FCSTD DOCUMENT  (FreeCAD 0.21R33771 (Git))
Label: RING0
License: All rights reserved
LicenseURL: http://en.wikipedia.org/wiki/All_rights_reserved
objects: Part::Part2DObjectPython×336, App::FeaturePython×24, App::DocumentObjectGroup×1
note: 336 computed .brp shape members not serialized (recipe doc carries the construction recipe); baked Part::Feature solids carry a one-line shape summary decoded from their .brp

FEATURE [Part::Part2DObjectPython] Rectangle  # Draft 2D object (typed FeaturePython)
  Area = 0
  ChamferSize = 0
  Columns = 1
  FilletRadius = 0
  Height = 8.42
  Length = 8.42
  MakeFace = false
  Placement = pos=(267.255,-49.5968,0) rot=(0,0,1;6.11518rad)
  Rows = 1
FEATURE [Part::Part2DObjectPython] Circle  # Draft 2D object (typed FeaturePython)
  Area = 0
  FirstAngle = 0
  LastAngle = 0
  MakeFace = false
  Placement = pos=(267.959,-45.446,0) rot=(0,0,1;6.11518rad)
  Radius = 1
FEATURE [Part::Part2DObjectPython] Rectangle001  # Draft 2D object (typed FeaturePython)
  Area = 0
  ChamferSize = 0
  Columns = 1
  FilletRadius = 0
  Height = 6
  Length = 6
  MakeFace = false
  Placement = pos=(269.11,-49.15,0) rot=(0,0,1;0rad)
  Rows = 1
FEATURE [App::FeaturePython] Text  # WARN: FeaturePython — macro-defined, semantics opaque (R4)
  Placement = pos=(270.79,-53.3517,0) rot=(0,0,-1;4.73892rad)
  Text = 0
FEATURE [App::FeaturePython] Text001  # WARN: FeaturePython — macro-defined, semantics opaque (R4)
  Placement = pos=(268.047,49.5386,0) rot=(0,0,1;2.6241rad)
  Text = 6.
FEATURE [Part::Part2DObjectPython] Circle001  # Draft 2D object (typed FeaturePython)
  Area = 3.14159
  FirstAngle = 0
  LastAngle = 0
  MakeFace = true
  Placement = pos=(276.11,-46.15,0) rot=(0,0,1;0rad)
  Radius = 1
FEATURE [Part::Part2DObjectPython] Rectangle002  # Draft 2D object (typed FeaturePython)
  Area = 0
  ChamferSize = 0
  Columns = 1
  FilletRadius = 0
  Height = 8.42
  Length = 8.42
  MakeFace = false
  Placement = pos=(269.616,-34.563,0) rot=(0,0,1;6.17118rad)
  Rows = 1
FEATURE [Part::Part2DObjectPython] Circle002  # Draft 2D object (typed FeaturePython)
  Area = 0
  FirstAngle = 0
  LastAngle = 0
  MakeFace = false
  Placement = pos=(270.086,-30.3794,0) rot=(0,0,1;6.17118rad)
  Radius = 1
FEATURE [Part::Part2DObjectPython] Rectangle003  # Draft 2D object (typed FeaturePython)
  Area = 0
  ChamferSize = 0
  Columns = 1
  FilletRadius = 0
  Height = 6
  Length = 6
  MakeFace = false
  Placement = pos=(271.27,-33.85,0) rot=(0,0,1;0rad)
  Rows = 1
FEATURE [Part::Part2DObjectPython] Circle003  # Draft 2D object (typed FeaturePython)
  Area = 3.14159
  FirstAngle = 0
  LastAngle = 0
  MakeFace = true
  Placement = pos=(278.27,-30.85,0) rot=(0,0,1;0rad)
  Radius = 1
FEATURE [Part::Part2DObjectPython] Rectangle004  # Draft 2D object (typed FeaturePython)
  Area = 0
  ChamferSize = 0
  Columns = 1
  FilletRadius = 0
  Height = 8.42
  Length = 8.42
  MakeFace = false
  Placement = pos=(271.131,-19.4177,0) rot=(0,0,1;6.22718rad)
  Rows = 1
FEATURE [Part::Part2DObjectPython] Circle004  # Draft 2D object (typed FeaturePython)
  Area = 0
  FirstAngle = 0
  LastAngle = 0
  MakeFace = false
  Placement = pos=(271.367,-15.2143,0) rot=(0,0,1;6.22718rad)
  Radius = 1
FEATURE [Part::Part2DObjectPython] Rectangle005  # Draft 2D object (typed FeaturePython)
  Area = 0
  ChamferSize = 0
  Columns = 1
  FilletRadius = 0
  Height = 6
  Length = 6
  MakeFace = false
  Placement = pos=(279.554,-16.9094,0) rot=(0,0,1;2.00503rad)
  Rows = 1
FEATURE [Part::Part2DObjectPython] Circle005  # Draft 2D object (typed FeaturePython)
  Area = 3.14159
  FirstAngle = 0
  LastAngle = 0
  MakeFace = true
  Placement = pos=(273.887,-11.8212,0) rot=(0,0,1;2.00503rad)
  Radius = 1
FEATURE [Part::Part2DObjectPython] Rectangle006  # Draft 2D object (typed FeaturePython)
  Area = 0
  ChamferSize = 0
  Columns = 1
  FilletRadius = 0
  Height = 8.42
  Length = 8.42
  MakeFace = false
  Placement = pos=(271.79,-4.21,0) rot=(0,0,1;0rad)
  Rows = 1
FEATURE [Part::Part2DObjectPython] Circle006  # Draft 2D object (typed FeaturePython)
  Area = 0
  FirstAngle = 0
  LastAngle = 0
  MakeFace = false
  Placement = pos=(271.79,0,0) rot=(0,0,1;0rad)
  Radius = 1
FEATURE [Part::Part2DObjectPython] Rectangle007  # Draft 2D object (typed FeaturePython)
  Area = 0
  ChamferSize = 0
  Columns = 1
  FilletRadius = 0
  Height = 6
  Length = 6
  MakeFace = false
  Placement = pos=(279.954,-1.537,0) rot=(0,0,1;1.98549rad)
  Rows = 1
FEATURE [Part::Part2DObjectPython] Circle007  # Draft 2D object (typed FeaturePython)
  Area = 3.14159
  FirstAngle = 0
  LastAngle = 0
  MakeFace = true
  Placement = pos=(274.388,3.66096,0) rot=(0,0,1;1.98549rad)
  Radius = 1
FEATURE [Part::Part2DObjectPython] Rectangle008  # Draft 2D object (typed FeaturePython)
  Area = 0
  ChamferSize = 0
  Columns = 1
  FilletRadius = 0
  Height = 8.42
  Length = 8.42
  MakeFace = false
  Placement = pos=(271.602,11.0109,0) rot=(0,0,1;0.056007rad)
  Rows = 1
FEATURE [Part::Part2DObjectPython] Circle008  # Draft 2D object (typed FeaturePython)
  Area = 0
  FirstAngle = 0
  LastAngle = 0
  MakeFace = false
  Placement = pos=(271.367,15.2143,0) rot=(0,0,1;0.056007rad)
  Radius = 1
FEATURE [Part::Part2DObjectPython] Rectangle009  # Draft 2D object (typed FeaturePython)
  Area = 0
  ChamferSize = 0
  Columns = 1
  FilletRadius = 0
  Height = 6
  Length = 6
  MakeFace = false
  Placement = pos=(279.425,13.6792,0) rot=(0,0,1;1.92562rad)
  Rows = 1
FEATURE [Part::Part2DObjectPython] Circle009  # Draft 2D object (typed FeaturePython)
  Area = 3.14159
  FirstAngle = 0
  LastAngle = 0
  MakeFace = true
  Placement = pos=(274.18,19.2008,0) rot=(0,0,1;1.92562rad)
  Radius = 1
FEATURE [Part::Part2DObjectPython] Rectangle010  # Draft 2D object (typed FeaturePython)
  Area = 0
  ChamferSize = 0
  Columns = 1
  FilletRadius = 0
  Height = 8.42
  Length = 8.42
  MakeFace = false
  Placement = pos=(270.557,26.1958,0) rot=(0,0,1;0.11201rad)
  Rows = 1
FEATURE [Part::Part2DObjectPython] Circle010  # Draft 2D object (typed FeaturePython)
  Area = 0
  FirstAngle = 0
  LastAngle = 0
  MakeFace = false
  Placement = pos=(270.086,30.3794,0) rot=(0,0,1;0.11201rad)
  Radius = 1
FEATURE [Part::Part2DObjectPython] Rectangle011  # Draft 2D object (typed FeaturePython)
  Area = 0
  ChamferSize = 0
  Columns = 1
  FilletRadius = 0
  Height = 6
  Length = 6
  MakeFace = false
  Placement = pos=(277.955,28.7473,0) rot=(0,0,1;1.83766rad)
  Rows = 1
FEATURE [Part::Part2DObjectPython] Circle011  # Draft 2D object (typed FeaturePython)
  Area = 3.14159
  FirstAngle = 0
  LastAngle = 0
  MakeFace = true
  Placement = pos=(273.215,34.7084,0) rot=(0,0,1;1.83766rad)
  Radius = 1
FEATURE [Part::Part2DObjectPython] Rectangle012  # Draft 2D object (typed FeaturePython)
  Area = 0
  ChamferSize = 0
  Columns = 1
  FilletRadius = 0
  Height = 8.42
  Length = 8.42
  MakeFace = false
  Placement = pos=(268.663,41.2953,0) rot=(0,0,1;0.168002rad)
  Rows = 1
FEATURE [Part::Part2DObjectPython] Circle012  # Draft 2D object (typed FeaturePython)
  Area = 0
  FirstAngle = 0
  LastAngle = 0
  MakeFace = false
  Placement = pos=(267.959,45.446,0) rot=(0,0,1;0.168002rad)
  Radius = 1
FEATURE [Part::Part2DObjectPython] Rectangle013  # Draft 2D object (typed FeaturePython)
  Area = 0
  ChamferSize = 0
  Columns = 1
  FilletRadius = 0
  Height = 6
  Length = 6
  MakeFace = false
  Placement = pos=(275.609,43.7506,0) rot=(0,0,1;1.7551rad)
  Rows = 1
FEATURE [Part::Part2DObjectPython] Circle013  # Draft 2D object (typed FeaturePython)
  Area = 3.14159
  FirstAngle = 0
  LastAngle = 0
  MakeFace = true
  Placement = pos=(271.377,50.0823,0) rot=(0,0,1;1.7551rad)
  Radius = 1
FEATURE [Part::Part2DObjectPython] Rectangle014  # Draft 2D object (typed FeaturePython)
  Area = 0
  ChamferSize = 0
  Columns = 1
  FilletRadius = 0
  Height = 8.42
  Length = 8.42
  MakeFace = false
  Placement = pos=(256.249,90.6777,0) rot=(0,0,1;0.355603rad)
  Rows = 1
FEATURE [Part::Part2DObjectPython] Circle014  # Draft 2D object (typed FeaturePython)
  Area = 0
  FirstAngle = 0
  LastAngle = 0
  MakeFace = false
  Placement = pos=(254.783,94.6243,0) rot=(0,0,1;0.355603rad)
  Radius = 1
FEATURE [Part::Part2DObjectPython] Rectangle015  # Draft 2D object (typed FeaturePython)
  Area = 0
  ChamferSize = 0
  Columns = 1
  FilletRadius = 0
  Height = 6
  Length = 6
  MakeFace = false
  Placement = pos=(262.426,94.0073,0) rot=(0,0,1;1.84307rad)
  Rows = 1
FEATURE [App::FeaturePython] Text002  # WARN: FeaturePython — macro-defined, semantics opaque (R4)
  Placement = pos=(261.188,89.1931,0) rot=(0,0,-1;4.21532rad)
  Text = 0
FEATURE [App::FeaturePython] Text003  # WARN: FeaturePython — macro-defined, semantics opaque (R4)
  Placement = pos=(207.363,176.926,0) rot=(0,0,1;3.1477rad)
  Text = 7
FEATURE [Part::Part2DObjectPython] Circle015  # Draft 2D object (typed FeaturePython)
  Area = 3.14159
  FirstAngle = 0
  LastAngle = 0
  MakeFace = true
  Placement = pos=(257.654,99.9427,0) rot=(0,0,1;1.84307rad)
  Radius = 1
FEATURE [Part::Part2DObjectPython] Rectangle016  # Draft 2D object (typed FeaturePython)
  Area = 0
  ChamferSize = 0
  Columns = 1
  FilletRadius = 0
  Height = 8.42
  Length = 8.42
  MakeFace = false
  Placement = pos=(250.776,104.877,0) rot=(0,0,1;0.411595rad)
  Rows = 1
FEATURE [Part::Part2DObjectPython] Circle016  # Draft 2D object (typed FeaturePython)
  Area = 0
  FirstAngle = 0
  LastAngle = 0
  MakeFace = false
  Placement = pos=(249.092,108.736,0) rot=(0,0,1;0.411595rad)
  Radius = 1
FEATURE [Part::Part2DObjectPython] Rectangle017  # Draft 2D object (typed FeaturePython)
  Area = 0
  ChamferSize = 0
  Columns = 1
  FilletRadius = 0
  Height = 6
  Length = 6
  MakeFace = false
  Placement = pos=(257.005,109.172,0) rot=(0,0,1;2.05774rad)
  Rows = 1
FEATURE [Part::Part2DObjectPython] Circle017  # Draft 2D object (typed FeaturePython)
  Area = 3.14159
  FirstAngle = 0
  LastAngle = 0
  MakeFace = true
  Placement = pos=(251.078,113.955,0) rot=(0,0,1;2.05774rad)
  Radius = 1
FEATURE [Part::Part2DObjectPython] Rectangle018  # Draft 2D object (typed FeaturePython)
  Area = 0
  ChamferSize = 0
  Columns = 1
  FilletRadius = 0
  Height = 8.42
  Length = 8.42
  MakeFace = false
  Placement = pos=(244.51,118.754,0) rot=(0,0,1;0.467617rad)
  Rows = 1
FEATURE [Part::Part2DObjectPython] Circle018  # Draft 2D object (typed FeaturePython)
  Area = 0
  FirstAngle = 0
  LastAngle = 0
  MakeFace = false
  Placement = pos=(242.612,122.512,0) rot=(0,0,1;0.467617rad)
  Radius = 1
FEATURE [Part::Part2DObjectPython] Rectangle019  # Draft 2D object (typed FeaturePython)
  Area = 0
  ChamferSize = 0
  Columns = 1
  FilletRadius = 0
  Height = 6
  Length = 6
  MakeFace = false
  Placement = pos=(250.401,125.732,0) rot=(0,0,1;2.67315rad)
  Rows = 1
FEATURE [Part::Part2DObjectPython] Circle019  # Draft 2D object (typed FeaturePython)
  Area = 3.14159
  FirstAngle = 0
  LastAngle = 0
  MakeFace = true
  Placement = pos=(242.801,126.216,0) rot=(0,0,1;2.67315rad)
  Radius = 1
FEATURE [Part::Part2DObjectPython] Rectangle020  # Draft 2D object (typed FeaturePython)
  Area = 0
  ChamferSize = 0
  Columns = 1
  FilletRadius = 0
  Height = 8.42
  Length = 8.42
  MakeFace = false
  Placement = pos=(237.479,132.249,0) rot=(0,0,1;0.523604rad)
  Rows = 1
FEATURE [Part::Part2DObjectPython] Circle020  # Draft 2D object (typed FeaturePython)
  Area = 0
  FirstAngle = 0
  LastAngle = 0
  MakeFace = false
  Placement = pos=(235.374,135.895,0) rot=(0,0,1;0.523604rad)
  Radius = 1
FEATURE [Part::Part2DObjectPython] Rectangle021  # Draft 2D object (typed FeaturePython)
  Area = 0
  ChamferSize = 0
  Columns = 1
  FilletRadius = 0
  Height = 6
  Length = 6
  MakeFace = false
  Placement = pos=(237.816,142.068,0) rot=(0,0,1;4.21462rad)
  Rows = 1
FEATURE [Part::Part2DObjectPython] Circle021  # Draft 2D object (typed FeaturePython)
  Area = 3.14159
  FirstAngle = 0
  LastAngle = 0
  MakeFace = true
  Placement = pos=(237.11,134.485,0) rot=(0,0,1;4.21462rad)
  Radius = 1
FEATURE [Part::Part2DObjectPython] Rectangle022  # Draft 2D object (typed FeaturePython)
  Area = 0
  ChamferSize = 0
  Columns = 1
  FilletRadius = 0
  Height = 8.42
  Length = 8.42
  MakeFace = false
  Placement = pos=(229.703,145.332,0) rot=(0,0,1;0.579601rad)
  Rows = 1
FEATURE [Part::Part2DObjectPython] Circle022  # Draft 2D object (typed FeaturePython)
  Area = 0
  FirstAngle = 0
  LastAngle = 0
  MakeFace = false
  Placement = pos=(227.398,148.854,0) rot=(0,0,1;0.579601rad)
  Radius = 1
FEATURE [Part::Part2DObjectPython] Rectangle023  # Draft 2D object (typed FeaturePython)
  Area = 0
  ChamferSize = 0
  Columns = 1
  FilletRadius = 0
  Height = 6
  Length = 6
  MakeFace = false
  Placement = pos=(227.695,153.917,0) rot=(0,0,1;4.7904rad)
  Rows = 1
FEATURE [Part::Part2DObjectPython] Circle023  # Draft 2D object (typed FeaturePython)
  Area = 3.14159
  FirstAngle = 0
  LastAngle = 0
  MakeFace = true
  Placement = pos=(231.232,147.172,0) rot=(0,0,1;4.7904rad)
  Radius = 1
FEATURE [Part::Part2DObjectPython] Rectangle024  # Draft 2D object (typed FeaturePython)
  Area = 0
  ChamferSize = 0
  Columns = 1
  FilletRadius = 0
  Height = 8.42
  Length = 8.42
  MakeFace = false
  Placement = pos=(221.211,157.963,0) rot=(0,0,1;0.635602rad)
  Rows = 1
FEATURE [Part::Part2DObjectPython] Circle024  # Draft 2D object (typed FeaturePython)
  Area = 0
  FirstAngle = 0
  LastAngle = 0
  MakeFace = false
  Placement = pos=(218.712,161.351,0) rot=(0,0,1;0.635602rad)
  Radius = 1
FEATURE [Part::Part2DObjectPython] Rectangle025  # Draft 2D object (typed FeaturePython)
  Area = 0
  ChamferSize = 0
  Columns = 1
  FilletRadius = 0
  Height = 6
  Length = 6
  MakeFace = false
  Placement = pos=(218.268,165.67,0) rot=(0,0,1;5.0543rad)
  Rows = 1
FEATURE [Part::Part2DObjectPython] Circle025  # Draft 2D object (typed FeaturePython)
  Area = 3.14159
  FirstAngle = 0
  LastAngle = 0
  MakeFace = true
  Placement = pos=(223.441,160.082,0) rot=(0,0,1;5.0543rad)
  Radius = 1
FEATURE [Part::Part2DObjectPython] Rectangle026  # Draft 2D object (typed FeaturePython)
  Area = 0
  ChamferSize = 0
  Columns = 1
  FilletRadius = 0
  Height = 8.42
  Length = 8.42
  MakeFace = false
  Placement = pos=(212.022,170.092,0) rot=(0,0,1;0.691593rad)
  Rows = 1
FEATURE [Part::Part2DObjectPython] Circle026  # Draft 2D object (typed FeaturePython)
  Area = 0
  FirstAngle = 0
  LastAngle = 0
  MakeFace = false
  Placement = pos=(209.337,173.335,0) rot=(0,0,1;0.691593rad)
  Radius = 1
FEATURE [Part::Part2DObjectPython] Rectangle027  # Draft 2D object (typed FeaturePython)
  Area = 0
  ChamferSize = 0
  Columns = 1
  FilletRadius = 0
  Height = 6
  Length = 6
  MakeFace = false
  Placement = pos=(208.466,177.056,0) rot=(0,0,1;5.251rad)
  Rows = 1
FEATURE [Part::Part2DObjectPython] Circle027  # Draft 2D object (typed FeaturePython)
  Area = 3.14159
  FirstAngle = 0
  LastAngle = 0
  MakeFace = true
  Placement = pos=(214.632,172.586,0) rot=(0,0,1;5.251rad)
  Radius = 1
FEATURE [Part::Part2DObjectPython] Rectangle028  # Draft 2D object (typed FeaturePython)
  Area = 0
  ChamferSize = 0
  Columns = 1
  FilletRadius = 0
  Height = 8.42
  Length = 8.42
  MakeFace = false
  Placement = pos=(176.578,206.652,0) rot=(0,0,1;0.879203rad)
  Rows = 1
FEATURE [Part::Part2DObjectPython] Circle028  # Draft 2D object (typed FeaturePython)
  Area = 0
  FirstAngle = 0
  LastAngle = 0
  MakeFace = false
  Placement = pos=(173.335,209.337,0) rot=(0,0,1;0.879203rad)
  Radius = 1
FEATURE [Part::Part2DObjectPython] Rectangle029  # Draft 2D object (typed FeaturePython)
  Area = 0
  ChamferSize = 0
  Columns = 1
  FilletRadius = 0
  Height = 6
  Length = 6
  MakeFace = false
  Placement = pos=(171.985,211.268,0) rot=(0,0,1;5.81229rad)
  Rows = 1
FEATURE [App::FeaturePython] Text004  # WARN: FeaturePython — macro-defined, semantics opaque (R4)
  Placement = pos=(181.597,207.836,0) rot=(0,0,-1;3.69172rad)
  Text = 0
FEATURE [App::FeaturePython] Text005  # WARN: FeaturePython — macro-defined, semantics opaque (R4)
  Placement = pos=(91.1209,256.902,0) rot=(0,0,1;3.6713rad)
  Text = 8
FEATURE [Part::Part2DObjectPython] Circle029  # Draft 2D object (typed FeaturePython)
  Area = 3.14159
  FirstAngle = 0
  LastAngle = 0
  MakeFace = true
  Placement = pos=(179.585,210.765,0) rot=(0,0,1;5.81229rad)
  Radius = 1
FEATURE [Part::Part2DObjectPython] Rectangle030  # Draft 2D object (typed FeaturePython)
  Area = 0
  ChamferSize = 0
  Columns = 1
  FilletRadius = 0
  Height = 8.42
  Length = 8.42
  MakeFace = false
  Placement = pos=(164.739,216.213,0) rot=(0,0,1;0.935194rad)
  Rows = 1
FEATURE [Part::Part2DObjectPython] Circle030  # Draft 2D object (typed FeaturePython)
  Area = 0
  FirstAngle = 0
  LastAngle = 0
  MakeFace = false
  Placement = pos=(161.351,218.712,0) rot=(0,0,1;0.935194rad)
  Radius = 1
FEATURE [Part::Part2DObjectPython] Rectangle031  # Draft 2D object (typed FeaturePython)
  Area = 0
  ChamferSize = 0
  Columns = 1
  FilletRadius = 0
  Height = 6
  Length = 6
  MakeFace = false
  Placement = pos=(160.075,220.163,0) rot=(0,0,1;5.97182rad)
  Rows = 1
FEATURE [Part::Part2DObjectPython] Circle031  # Draft 2D object (typed FeaturePython)
  Area = 3.14159
  FirstAngle = 0
  LastAngle = 0
  MakeFace = true
  Placement = pos=(167.658,220.875,0) rot=(0,0,1;5.97182rad)
  Radius = 1
FEATURE [Part::Part2DObjectPython] Rectangle032  # Draft 2D object (typed FeaturePython)
  Area = 0
  ChamferSize = 0
  Columns = 1
  FilletRadius = 0
  Height = 8.42
  Length = 8.42
  MakeFace = false
  Placement = pos=(152.377,225.092,0) rot=(0,0,1;0.991195rad)
  Rows = 1
FEATURE [Part::Part2DObjectPython] Circle032  # Draft 2D object (typed FeaturePython)
  Area = 0
  FirstAngle = 0
  LastAngle = 0
  MakeFace = false
  Placement = pos=(148.854,227.398,0) rot=(0,0,1;0.991195rad)
  Radius = 1
FEATURE [Part::Part2DObjectPython] Rectangle033  # Draft 2D object (typed FeaturePython)
  Area = 0
  ChamferSize = 0
  Columns = 1
  FilletRadius = 0
  Height = 6
  Length = 6
  MakeFace = false
  Placement = pos=(147.739,228.41,0) rot=(0,0,1;6.13082rad)
  Rows = 1
FEATURE [Part::Part2DObjectPython] Circle033  # Draft 2D object (typed FeaturePython)
  Area = 3.14159
  FirstAngle = 0
  LastAngle = 0
  MakeFace = true
  Placement = pos=(155.114,230.313,0) rot=(0,0,1;6.13082rad)
  Radius = 1
FEATURE [Part::Part2DObjectPython] Rectangle034  # Draft 2D object (typed FeaturePython)
  Area = 0
  ChamferSize = 0
  Columns = 1
  FilletRadius = 0
  Height = 8.42
  Length = 8.42
  MakeFace = false
  Placement = pos=(139.541,233.269,0) rot=(0,0,1;1.04719rad)
  Rows = 1
FEATURE [Part::Part2DObjectPython] Circle034  # Draft 2D object (typed FeaturePython)
  Area = 0
  FirstAngle = 0
  LastAngle = 0
  MakeFace = false
  Placement = pos=(135.895,235.374,0) rot=(0,0,1;1.04719rad)
  Radius = 1
FEATURE [Part::Part2DObjectPython] Rectangle035  # Draft 2D object (typed FeaturePython)
  Area = 0
  ChamferSize = 0
  Columns = 1
  FilletRadius = 0
  Height = 6
  Length = 6
  MakeFace = false
  Placement = pos=(134.999,236.021,0) rot=(0,0,1;6.28284rad)
  Rows = 1
FEATURE [Part::Part2DObjectPython] Circle035  # Draft 2D object (typed FeaturePython)
  Area = 3.14159
  FirstAngle = 0
  LastAngle = 0
  MakeFace = true
  Placement = pos=(142,239.019,0) rot=(0,0,1;6.28284rad)
  Radius = 1
FEATURE [Part::Part2DObjectPython] Rectangle036  # Draft 2D object (typed FeaturePython)
  Area = 0
  ChamferSize = 0
  Columns = 1
  FilletRadius = 0
  Height = 8.42
  Length = 8.42
  MakeFace = false
  Placement = pos=(126.27,240.714,0) rot=(0,0,1;1.10318rad)
  Rows = 1
FEATURE [Part::Part2DObjectPython] Circle036  # Draft 2D object (typed FeaturePython)
  Area = 0
  FirstAngle = 0
  LastAngle = 0
  MakeFace = false
  Placement = pos=(122.512,242.612,0) rot=(0,0,1;1.10318rad)
  Radius = 1
FEATURE [Part::Part2DObjectPython] Rectangle037  # Draft 2D object (typed FeaturePython)
  Area = 0
  ChamferSize = 0
  Columns = 1
  FilletRadius = 0
  Height = 6
  Length = 6
  MakeFace = false
  Placement = pos=(121.98,242.893,0) rot=(0,0,1;0.175406rad)
  Rows = 1
FEATURE [Part::Part2DObjectPython] Circle037  # Draft 2D object (typed FeaturePython)
  Area = 3.14159
  FirstAngle = 0
  LastAngle = 0
  MakeFace = true
  Placement = pos=(128.349,247.068,0) rot=(0,0,1;0.175406rad)
  Radius = 1
FEATURE [Part::Part2DObjectPython] Rectangle038  # Draft 2D object (typed FeaturePython)
  Area = 0
  ChamferSize = 0
  Columns = 1
  FilletRadius = 0
  Height = 8.42
  Length = 8.42
  MakeFace = false
  Placement = pos=(112.594,247.407,0) rot=(0,0,1;1.1592rad)
  Rows = 1
FEATURE [Part::Part2DObjectPython] Circle038  # Draft 2D object (typed FeaturePython)
  Area = 0
  FirstAngle = 0
  LastAngle = 0
  MakeFace = false
  Placement = pos=(108.736,249.092,0) rot=(0,0,1;1.1592rad)
  Radius = 1
FEATURE [Part::Part2DObjectPython] Rectangle039  # Draft 2D object (typed FeaturePython)
  Area = 0
  ChamferSize = 0
  Columns = 1
  FilletRadius = 0
  Height = 6
  Length = 6
  MakeFace = false
  Placement = pos=(107.42,249.95,0) rot=(0,0,1;0rad)
  Rows = 1
FEATURE [Part::Part2DObjectPython] Circle039  # Draft 2D object (typed FeaturePython)
  Area = 3.14159
  FirstAngle = 0
  LastAngle = 0
  MakeFace = true
  Placement = pos=(114.42,252.95,0) rot=(0,0,1;0rad)
  Radius = 1
FEATURE [Part::Part2DObjectPython] Rectangle040  # Draft 2D object (typed FeaturePython)
  Area = 0
  ChamferSize = 0
  Columns = 1
  FilletRadius = 0
  Height = 8.42
  Length = 8.42
  MakeFace = false
  Placement = pos=(98.5709,253.318,0) rot=(0,0,1;1.21519rad)
  Rows = 1
FEATURE [Part::Part2DObjectPython] Circle040  # Draft 2D object (typed FeaturePython)
  Area = 0
  FirstAngle = 0
  LastAngle = 0
  MakeFace = false
  Placement = pos=(94.6243,254.783,0) rot=(0,0,1;1.21519rad)
  Radius = 1
FEATURE [Part::Part2DObjectPython] Rectangle041  # Draft 2D object (typed FeaturePython)
  Area = 0
  ChamferSize = 0
  Columns = 1
  FilletRadius = 0
  Height = 6
  Length = 6
  MakeFace = false
  Placement = pos=(93.09,255.73,0) rot=(0,0,1;0rad)
  Rows = 1
FEATURE [Part::Part2DObjectPython] Circle041  # Draft 2D object (typed FeaturePython)
  Area = 3.14159
  FirstAngle = 0
  LastAngle = 0
  MakeFace = true
  Placement = pos=(100.09,258.73,0) rot=(0,0,1;0rad)
  Radius = 1
FEATURE [Part::Part2DObjectPython] Rectangle042  # Draft 2D object (typed FeaturePython)
  Area = 0
  ChamferSize = 0
  Columns = 1
  FilletRadius = 0
  Height = 8.42
  Length = 8.42
  MakeFace = false
  Placement = pos=(49.5968,267.255,0) rot=(0,0,1;1.40279rad)
  Rows = 1
FEATURE [Part::Part2DObjectPython] Circle042  # Draft 2D object (typed FeaturePython)
  Area = 0
  FirstAngle = 0
  LastAngle = 0
  MakeFace = false
  Placement = pos=(45.446,267.959,0) rot=(0,0,1;1.40279rad)
  Radius = 1
FEATURE [Part::Part2DObjectPython] Rectangle043  # Draft 2D object (typed FeaturePython)
  Area = 0
  ChamferSize = 0
  Columns = 1
  FilletRadius = 0
  Height = 6
  Length = 6
  MakeFace = false
  Placement = pos=(43.15,269.11,0) rot=(0,0,1;0rad)
  Rows = 1
FEATURE [App::FeaturePython] Text006  # WARN: FeaturePython — macro-defined, semantics opaque (R4)
  Placement = pos=(53.3517,270.79,0) rot=(0,0,-1;3.16812rad)
  Text = 0
FEATURE [App::FeaturePython] Text007  # WARN: FeaturePython — macro-defined, semantics opaque (R4)
  Placement = pos=(-49.5386,268.047,0) rot=(0,0,1;4.1949rad)
  Text = 9
FEATURE [Part::Part2DObjectPython] Circle043  # Draft 2D object (typed FeaturePython)
  Area = 3.14159
  FirstAngle = 0
  LastAngle = 0
  MakeFace = true
  Placement = pos=(50.15,272.11,0) rot=(0,0,1;0rad)
  Radius = 1
FEATURE [Part::Part2DObjectPython] Rectangle044  # Draft 2D object (typed FeaturePython)
  Area = 0
  ChamferSize = 0
  Columns = 1
  FilletRadius = 0
  Height = 8.42
  Length = 8.42
  MakeFace = false
  Placement = pos=(34.563,269.616,0) rot=(0,0,1;1.45879rad)
  Rows = 1
FEATURE [Part::Part2DObjectPython] Circle044  # Draft 2D object (typed FeaturePython)
  Area = 0
  FirstAngle = 0
  LastAngle = 0
  MakeFace = false
  Placement = pos=(30.3794,270.086,0) rot=(0,0,1;1.45879rad)
  Radius = 1
FEATURE [Part::Part2DObjectPython] Rectangle045  # Draft 2D object (typed FeaturePython)
  Area = 0
  ChamferSize = 0
  Columns = 1
  FilletRadius = 0
  Height = 6
  Length = 6
  MakeFace = false
  Placement = pos=(27.85,271.27,0) rot=(0,0,1;0rad)
  Rows = 1
FEATURE [Part::Part2DObjectPython] Circle045  # Draft 2D object (typed FeaturePython)
  Area = 3.14159
  FirstAngle = 0
  LastAngle = 0
  MakeFace = true
  Placement = pos=(34.85,274.27,0) rot=(0,0,1;0rad)
  Radius = 1
FEATURE [Part::Part2DObjectPython] Rectangle046  # Draft 2D object (typed FeaturePython)
  Area = 0
  ChamferSize = 0
  Columns = 1
  FilletRadius = 0
  Height = 8.42
  Length = 8.42
  MakeFace = false
  Placement = pos=(19.4177,271.131,0) rot=(0,0,1;1.51479rad)
  Rows = 1
FEATURE [Part::Part2DObjectPython] Circle046  # Draft 2D object (typed FeaturePython)
  Area = 0
  FirstAngle = 0
  LastAngle = 0
  MakeFace = false
  Placement = pos=(15.2143,271.367,0) rot=(0,0,1;1.51479rad)
  Radius = 1
FEATURE [Part::Part2DObjectPython] Rectangle047  # Draft 2D object (typed FeaturePython)
  Area = 0
  ChamferSize = 0
  Columns = 1
  FilletRadius = 0
  Height = 6
  Length = 6
  MakeFace = false
  Placement = pos=(12.45,272.57,0) rot=(0,0,1;0rad)
  Rows = 1
FEATURE [Part::Part2DObjectPython] Circle047  # Draft 2D object (typed FeaturePython)
  Area = 3.14159
  FirstAngle = 0
  LastAngle = 0
  MakeFace = true
  Placement = pos=(19.45,275.57,0) rot=(0,0,1;0rad)
  Radius = 1
FEATURE [Part::Part2DObjectPython] Rectangle048  # Draft 2D object (typed FeaturePython)
  Area = 0
  ChamferSize = 0
  Columns = 1
  FilletRadius = 0
  Height = 8.42
  Length = 8.42
  MakeFace = false
  Placement = pos=(4.21,271.79,0) rot=(0,0,1;1.5708rad)
  Rows = 1
FEATURE [Part::Part2DObjectPython] Circle048  # Draft 2D object (typed FeaturePython)
  Area = 0
  FirstAngle = 0
  LastAngle = 0
  MakeFace = false
  Placement = pos=(0,271.79,0) rot=(0,0,1;1.5708rad)
  Radius = 1
FEATURE [Part::Part2DObjectPython] Rectangle049  # Draft 2D object (typed FeaturePython)
  Area = 0
  ChamferSize = 0
  Columns = 1
  FilletRadius = 0
  Height = 6
  Length = 6
  MakeFace = false
  Placement = pos=(-3,273,0) rot=(0,0,1;0rad)
  Rows = 1
FEATURE [Part::Part2DObjectPython] Circle049  # Draft 2D object (typed FeaturePython)
  Area = 3.14159
  FirstAngle = 0
  LastAngle = 0
  MakeFace = true
  Placement = pos=(4,276,0) rot=(0,0,1;0rad)
  Radius = 1
FEATURE [Part::Part2DObjectPython] Rectangle050  # Draft 2D object (typed FeaturePython)
  Area = 0
  ChamferSize = 0
  Columns = 1
  FilletRadius = 0
  Height = 8.42
  Length = 8.42
  MakeFace = false
  Placement = pos=(-11.0109,271.602,0) rot=(0,0,1;1.6268rad)
  Rows = 1
FEATURE [Part::Part2DObjectPython] Circle050  # Draft 2D object (typed FeaturePython)
  Area = 0
  FirstAngle = 0
  LastAngle = 0
  MakeFace = false
  Placement = pos=(-15.2143,271.367,0) rot=(0,0,1;1.6268rad)
  Radius = 1
FEATURE [Part::Part2DObjectPython] Rectangle051  # Draft 2D object (typed FeaturePython)
  Area = 0
  ChamferSize = 0
  Columns = 1
  FilletRadius = 0
  Height = 6
  Length = 6
  MakeFace = false
  Placement = pos=(-11.2074,275.547,0) rot=(0,0,1;2.35078rad)
  Rows = 1
FEATURE [Part::Part2DObjectPython] Circle051  # Draft 2D object (typed FeaturePython)
  Area = 3.14159
  FirstAngle = 0
  LastAngle = 0
  MakeFace = true
  Placement = pos=(-18.2631,278.414,0) rot=(0,0,1;2.35078rad)
  Radius = 1
FEATURE [Part::Part2DObjectPython] Rectangle052  # Draft 2D object (typed FeaturePython)
  Area = 0
  ChamferSize = 0
  Columns = 1
  FilletRadius = 0
  Height = 8.42
  Length = 8.42
  MakeFace = false
  Placement = pos=(-26.1958,270.557,0) rot=(0,0,1;1.68281rad)
  Rows = 1
FEATURE [Part::Part2DObjectPython] Circle052  # Draft 2D object (typed FeaturePython)
  Area = 0
  FirstAngle = 0
  LastAngle = 0
  MakeFace = false
  Placement = pos=(-30.3794,270.086,0) rot=(0,0,1;1.68281rad)
  Radius = 1
FEATURE [Part::Part2DObjectPython] Rectangle053  # Draft 2D object (typed FeaturePython)
  Area = 0
  ChamferSize = 0
  Columns = 1
  FilletRadius = 0
  Height = 6
  Length = 6
  MakeFace = false
  Placement = pos=(-26.6143,274.513,0) rot=(0,0,1;2.41344rad)
  Rows = 1
FEATURE [Part::Part2DObjectPython] Circle053  # Draft 2D object (typed FeaturePython)
  Area = 3.14159
  FirstAngle = 0
  LastAngle = 0
  MakeFace = true
  Placement = pos=(-33.8356,276.932,0) rot=(0,0,1;2.41344rad)
  Radius = 1
FEATURE [Part::Part2DObjectPython] Rectangle054  # Draft 2D object (typed FeaturePython)
  Area = 0
  ChamferSize = 0
  Columns = 1
  FilletRadius = 0
  Height = 8.42
  Length = 8.42
  MakeFace = false
  Placement = pos=(-41.2953,268.663,0) rot=(0,0,1;1.7388rad)
  Rows = 1
FEATURE [Part::Part2DObjectPython] Circle054  # Draft 2D object (typed FeaturePython)
  Area = 0
  FirstAngle = 0
  LastAngle = 0
  MakeFace = false
  Placement = pos=(-45.446,267.959,0) rot=(0,0,1;1.7388rad)
  Radius = 1
FEATURE [Part::Part2DObjectPython] Rectangle055  # Draft 2D object (typed FeaturePython)
  Area = 0
  ChamferSize = 0
  Columns = 1
  FilletRadius = 0
  Height = 6
  Length = 6
  MakeFace = false
  Placement = pos=(-41.9327,272.573,0) rot=(0,0,1;2.46545rad)
  Rows = 1
FEATURE [Part::Part2DObjectPython] Circle055  # Draft 2D object (typed FeaturePython)
  Area = 3.14159
  FirstAngle = 0
  LastAngle = 0
  MakeFace = true
  Placement = pos=(-49.27,274.613,0) rot=(0,0,1;2.46545rad)
  Radius = 1
FEATURE [Part::Part2DObjectPython] Rectangle056  # Draft 2D object (typed FeaturePython)
  Area = 0
  ChamferSize = 0
  Columns = 1
  FilletRadius = 0
  Height = 8.42
  Length = 8.42
  MakeFace = false
  Placement = pos=(-90.6777,256.249,0) rot=(0,0,1;1.9264rad)
  Rows = 1
FEATURE [Part::Part2DObjectPython] Circle056  # Draft 2D object (typed FeaturePython)
  Area = 0
  FirstAngle = 0
  LastAngle = 0
  MakeFace = false
  Placement = pos=(-94.6243,254.783,0) rot=(0,0,1;1.9264rad)
  Radius = 1
FEATURE [Part::Part2DObjectPython] Rectangle057  # Draft 2D object (typed FeaturePython)
  Area = 0
  ChamferSize = 0
  Columns = 1
  FilletRadius = 0
  Height = 6
  Length = 6
  MakeFace = false
  Placement = pos=(-92.1068,260.191,0) rot=(0,0,1;2.7077rad)
  Rows = 1
FEATURE [App::FeaturePython] Text008  # WARN: FeaturePython — macro-defined, semantics opaque (R4)
  Placement = pos=(-89.1931,261.188,0) rot=(0,0,-1;2.64452rad)
  Text = 0
FEATURE [App::FeaturePython] Text009  # WARN: FeaturePython — macro-defined, semantics opaque (R4)
  Placement = pos=(-176.926,207.363,0) rot=(0,0,1;4.7185rad)
  Text = 10
FEATURE [Part::Part2DObjectPython] Circle057  # Draft 2D object (typed FeaturePython)
  Area = 3.14159
  FirstAngle = 0
  LastAngle = 0
  MakeFace = true
  Placement = pos=(-99.7194,260.412,0) rot=(0,0,1;2.7077rad)
  Radius = 1
FEATURE [Part::Part2DObjectPython] Rectangle058  # Draft 2D object (typed FeaturePython)
  Area = 0
  ChamferSize = 0
  Columns = 1
  FilletRadius = 0
  Height = 8.42
  Length = 8.42
  MakeFace = false
  Placement = pos=(-104.877,250.776,0) rot=(0,0,1;1.98239rad)
  Rows = 1
FEATURE [Part::Part2DObjectPython] Circle058  # Draft 2D object (typed FeaturePython)
  Area = 0
  FirstAngle = 0
  LastAngle = 0
  MakeFace = false
  Placement = pos=(-108.736,249.092,0) rot=(0,0,1;1.98239rad)
  Radius = 1
FEATURE [Part::Part2DObjectPython] Rectangle059  # Draft 2D object (typed FeaturePython)
  Area = 0
  ChamferSize = 0
  Columns = 1
  FilletRadius = 0
  Height = 6
  Length = 6
  MakeFace = false
  Placement = pos=(-106.607,254.81,0) rot=(0,0,1;2.80998rad)
  Rows = 1
FEATURE [Part::Part2DObjectPython] Circle059  # Draft 2D object (typed FeaturePython)
  Area = 3.14159
  FirstAngle = 0
  LastAngle = 0
  MakeFace = true
  Placement = pos=(-114.202,254.252,0) rot=(0,0,1;2.80998rad)
  Radius = 1
FEATURE [Part::Part2DObjectPython] Rectangle060  # Draft 2D object (typed FeaturePython)
  Area = 0
  ChamferSize = 0
  Columns = 1
  FilletRadius = 0
  Height = 8.42
  Length = 8.42
  MakeFace = false
  Placement = pos=(-118.754,244.51,0) rot=(0,0,1;2.03841rad)
  Rows = 1
FEATURE [Part::Part2DObjectPython] Circle060  # Draft 2D object (typed FeaturePython)
  Area = 0
  FirstAngle = 0
  LastAngle = 0
  MakeFace = false
  Placement = pos=(-122.512,242.612,0) rot=(0,0,1;2.03841rad)
  Radius = 1
FEATURE [Part::Part2DObjectPython] Rectangle061  # Draft 2D object (typed FeaturePython)
  Area = 0
  ChamferSize = 0
  Columns = 1
  FilletRadius = 0
  Height = 6
  Length = 6
  MakeFace = false
  Placement = pos=(-120.843,248.666,0) rot=(0,0,1;2.92814rad)
  Rows = 1
FEATURE [Part::Part2DObjectPython] Circle061  # Draft 2D object (typed FeaturePython)
  Area = 3.14159
  FirstAngle = 0
  LastAngle = 0
  MakeFace = true
  Placement = pos=(-128.319,247.217,0) rot=(0,0,1;2.92814rad)
  Radius = 1
FEATURE [Part::Part2DObjectPython] Rectangle062  # Draft 2D object (typed FeaturePython)
  Area = 0
  ChamferSize = 0
  Columns = 1
  FilletRadius = 0
  Height = 8.42
  Length = 8.42
  MakeFace = false
  Placement = pos=(-132.249,237.479,0) rot=(0,0,1;2.0944rad)
  Rows = 1
FEATURE [Part::Part2DObjectPython] Circle062  # Draft 2D object (typed FeaturePython)
  Area = 0
  FirstAngle = 0
  LastAngle = 0
  MakeFace = false
  Placement = pos=(-135.895,235.374,0) rot=(0,0,1;2.0944rad)
  Radius = 1
FEATURE [Part::Part2DObjectPython] Rectangle063  # Draft 2D object (typed FeaturePython)
  Area = 0
  ChamferSize = 0
  Columns = 1
  FilletRadius = 0
  Height = 6
  Length = 6
  MakeFace = false
  Placement = pos=(-134.775,241.777,0) rot=(0,0,1;3.06358rad)
  Rows = 1
FEATURE [Part::Part2DObjectPython] Circle063  # Draft 2D object (typed FeaturePython)
  Area = 3.14159
  FirstAngle = 0
  LastAngle = 0
  MakeFace = true
  Placement = pos=(-141.988,239.332,0) rot=(0,0,1;3.06358rad)
  Radius = 1
FEATURE [Part::Part2DObjectPython] Rectangle064  # Draft 2D object (typed FeaturePython)
  Area = 0
  ChamferSize = 0
  Columns = 1
  FilletRadius = 0
  Height = 8.42
  Length = 8.42
  MakeFace = false
  Placement = pos=(-145.332,229.703,0) rot=(0,0,1;2.1504rad)
  Rows = 1
FEATURE [Part::Part2DObjectPython] Circle064  # Draft 2D object (typed FeaturePython)
  Area = 0
  FirstAngle = 0
  LastAngle = 0
  MakeFace = false
  Placement = pos=(-148.854,227.398,0) rot=(0,0,1;2.1504rad)
  Radius = 1
FEATURE [Part::Part2DObjectPython] Rectangle065  # Draft 2D object (typed FeaturePython)
  Area = 0
  ChamferSize = 0
  Columns = 1
  FilletRadius = 0
  Height = 6
  Length = 6
  MakeFace = false
  Placement = pos=(-148.392,234.135,0) rot=(0,0,1;3.21612rad)
  Rows = 1
FEATURE [Part::Part2DObjectPython] Circle065  # Draft 2D object (typed FeaturePython)
  Area = 3.14159
  FirstAngle = 0
  LastAngle = 0
  MakeFace = true
  Placement = pos=(-155.149,230.622,0) rot=(0,0,1;3.21612rad)
  Radius = 1
FEATURE [Part::Part2DObjectPython] Rectangle066  # Draft 2D object (typed FeaturePython)
  Area = 0
  ChamferSize = 0
  Columns = 1
  FilletRadius = 0
  Height = 8.42
  Length = 8.42
  MakeFace = false
  Placement = pos=(-157.963,221.211,0) rot=(0,0,1;2.2064rad)
  Rows = 1
FEATURE [Part::Part2DObjectPython] Circle066  # Draft 2D object (typed FeaturePython)
  Area = 0
  FirstAngle = 0
  LastAngle = 0
  MakeFace = false
  Placement = pos=(-161.351,218.712,0) rot=(0,0,1;2.2064rad)
  Radius = 1
FEATURE [Part::Part2DObjectPython] Rectangle067  # Draft 2D object (typed FeaturePython)
  Area = 0
  ChamferSize = 0
  Columns = 1
  FilletRadius = 0
  Height = 6
  Length = 6
  MakeFace = false
  Placement = pos=(-161.674,225.742,0) rot=(0,0,1;3.38838rad)
  Rows = 1
FEATURE [Part::Part2DObjectPython] Circle067  # Draft 2D object (typed FeaturePython)
  Area = 3.14159
  FirstAngle = 0
  LastAngle = 0
  MakeFace = true
  Placement = pos=(-167.729,221.123,0) rot=(0,0,1;3.38838rad)
  Radius = 1
FEATURE [Part::Part2DObjectPython] Rectangle068  # Draft 2D object (typed FeaturePython)
  Area = 0
  ChamferSize = 0
  Columns = 1
  FilletRadius = 0
  Height = 8.42
  Length = 8.42
  MakeFace = false
  Placement = pos=(-170.092,212.022,0) rot=(0,0,1;2.26239rad)
  Rows = 1
FEATURE [Part::Part2DObjectPython] Circle068  # Draft 2D object (typed FeaturePython)
  Area = 0
  FirstAngle = 0
  LastAngle = 0
  MakeFace = false
  Placement = pos=(-173.335,209.337,0) rot=(0,0,1;2.26239rad)
  Radius = 1
FEATURE [Part::Part2DObjectPython] Rectangle069  # Draft 2D object (typed FeaturePython)
  Area = 0
  ChamferSize = 0
  Columns = 1
  FilletRadius = 0
  Height = 6
  Length = 6
  MakeFace = false
  Placement = pos=(-174.591,216.575,0) rot=(0,0,1;3.58351rad)
  Rows = 1
FEATURE [Part::Part2DObjectPython] Circle069  # Draft 2D object (typed FeaturePython)
  Area = 3.14159
  FirstAngle = 0
  LastAngle = 0
  MakeFace = true
  Placement = pos=(-179.636,210.869,0) rot=(0,0,1;3.58351rad)
  Radius = 1
FEATURE [Part::Part2DObjectPython] Rectangle070  # Draft 2D object (typed FeaturePython)
  Area = 0
  ChamferSize = 0
  Columns = 1
  FilletRadius = 0
  Height = 8.42
  Length = 8.42
  MakeFace = false
  Placement = pos=(-206.652,176.578,0) rot=(0,0,1;2.45rad)
  Rows = 1
FEATURE [Part::Part2DObjectPython] Circle070  # Draft 2D object (typed FeaturePython)
  Area = 0
  FirstAngle = 0
  LastAngle = 0
  MakeFace = false
  Placement = pos=(-209.337,173.335,0) rot=(0,0,1;2.45rad)
  Radius = 1
FEATURE [Part::Part2DObjectPython] Rectangle071  # Draft 2D object (typed FeaturePython)
  Area = 0
  ChamferSize = 0
  Columns = 1
  FilletRadius = 0
  Height = 6
  Length = 6
  MakeFace = false
  Placement = pos=(-215.58,173.02,0) rot=(0,0,1;0rad)
  Rows = 1
FEATURE [App::FeaturePython] Text010  # WARN: FeaturePython — macro-defined, semantics opaque (R4)
  Placement = pos=(-207.836,181.597,0) rot=(0,0,-1;2.12092rad)
  Text = 0
FEATURE [App::FeaturePython] Text011  # WARN: FeaturePython — macro-defined, semantics opaque (R4)
  Placement = pos=(-256.902,91.1209,0) rot=(0,0,1;5.2421rad)
  Text = 11
FEATURE [Part::Part2DObjectPython] Circle071  # Draft 2D object (typed FeaturePython)
  Area = 3.14159
  FirstAngle = 0
  LastAngle = 0
  MakeFace = true
  Placement = pos=(-208.58,176.02,0) rot=(0,0,1;0rad)
  Radius = 1
FEATURE [Part::Part2DObjectPython] Rectangle072  # Draft 2D object (typed FeaturePython)
  Area = 0
  ChamferSize = 0
  Columns = 1
  FilletRadius = 0
  Height = 8.42
  Length = 8.42
  MakeFace = false
  Placement = pos=(-216.213,164.739,0) rot=(0,0,1;2.50599rad)
  Rows = 1
FEATURE [Part::Part2DObjectPython] Circle072  # Draft 2D object (typed FeaturePython)
  Area = 0
  FirstAngle = 0
  LastAngle = 0
  MakeFace = false
  Placement = pos=(-218.712,161.351,0) rot=(0,0,1;2.50599rad)
  Radius = 1
FEATURE [Part::Part2DObjectPython] Rectangle073  # Draft 2D object (typed FeaturePython)
  Area = 0
  ChamferSize = 0
  Columns = 1
  FilletRadius = 0
  Height = 6
  Length = 6
  MakeFace = false
  Placement = pos=(-225.1,160.85,0) rot=(0,0,1;0rad)
  Rows = 1
FEATURE [Part::Part2DObjectPython] Circle073  # Draft 2D object (typed FeaturePython)
  Area = 3.14159
  FirstAngle = 0
  LastAngle = 0
  MakeFace = true
  Placement = pos=(-218.1,163.85,0) rot=(0,0,1;0rad)
  Radius = 1
FEATURE [Part::Part2DObjectPython] Rectangle074  # Draft 2D object (typed FeaturePython)
  Area = 0
  ChamferSize = 0
  Columns = 1
  FilletRadius = 0
  Height = 8.42
  Length = 8.42
  MakeFace = false
  Placement = pos=(-225.092,152.377,0) rot=(0,0,1;2.56199rad)
  Rows = 1
FEATURE [Part::Part2DObjectPython] Circle074  # Draft 2D object (typed FeaturePython)
  Area = 0
  FirstAngle = 0
  LastAngle = 0
  MakeFace = false
  Placement = pos=(-227.398,148.854,0) rot=(0,0,1;2.56199rad)
  Radius = 1
FEATURE [Part::Part2DObjectPython] Rectangle075  # Draft 2D object (typed FeaturePython)
  Area = 0
  ChamferSize = 0
  Columns = 1
  FilletRadius = 0
  Height = 6
  Length = 6
  MakeFace = false
  Placement = pos=(-235.027,152.225,0) rot=(0,0,1;5.24402rad)
  Rows = 1
FEATURE [Part::Part2DObjectPython] Circle075  # Draft 2D object (typed FeaturePython)
  Area = 3.14159
  FirstAngle = 0
  LastAngle = 0
  MakeFace = true
  Placement = pos=(-228.892,147.712,0) rot=(0,0,1;5.24402rad)
  Radius = 1
FEATURE [Part::Part2DObjectPython] Rectangle076  # Draft 2D object (typed FeaturePython)
  Area = 0
  ChamferSize = 0
  Columns = 1
  FilletRadius = 0
  Height = 8.42
  Length = 8.42
  MakeFace = false
  Placement = pos=(-233.269,139.541,0) rot=(0,0,1;2.61799rad)
  Rows = 1
FEATURE [Part::Part2DObjectPython] Circle076  # Draft 2D object (typed FeaturePython)
  Area = 0
  FirstAngle = 0
  LastAngle = 0
  MakeFace = false
  Placement = pos=(-235.374,135.895,0) rot=(0,0,1;2.61799rad)
  Radius = 1
FEATURE [Part::Part2DObjectPython] Rectangle077  # Draft 2D object (typed FeaturePython)
  Area = 0
  ChamferSize = 0
  Columns = 1
  FilletRadius = 0
  Height = 6
  Length = 6
  MakeFace = false
  Placement = pos=(-243.205,137.304,0) rot=(0,0,1;5.66255rad)
  Rows = 1
FEATURE [Part::Part2DObjectPython] Circle077  # Draft 2D object (typed FeaturePython)
  Area = 3.14159
  FirstAngle = 0
  LastAngle = 0
  MakeFace = true
  Placement = pos=(-235.766,135.674,0) rot=(0,0,1;5.66255rad)
  Radius = 1
FEATURE [Part::Part2DObjectPython] Rectangle078  # Draft 2D object (typed FeaturePython)
  Area = 0
  ChamferSize = 0
  Columns = 1
  FilletRadius = 0
  Height = 8.42
  Length = 8.42
  MakeFace = false
  Placement = pos=(-240.714,126.27,0) rot=(0,0,1;2.67397rad)
  Rows = 1
FEATURE [Part::Part2DObjectPython] Circle078  # Draft 2D object (typed FeaturePython)
  Area = 0
  FirstAngle = 0
  LastAngle = 0
  MakeFace = false
  Placement = pos=(-242.612,122.512,0) rot=(0,0,1;2.67397rad)
  Radius = 1
FEATURE [Part::Part2DObjectPython] Rectangle079  # Draft 2D object (typed FeaturePython)
  Area = 0
  ChamferSize = 0
  Columns = 1
  FilletRadius = 0
  Height = 6
  Length = 6
  MakeFace = false
  Placement = pos=(-249.949,122.131,0) rot=(0,0,1;6.06485rad)
  Rows = 1
FEATURE [Part::Part2DObjectPython] Circle079  # Draft 2D object (typed FeaturePython)
  Area = 3.14159
  FirstAngle = 0
  LastAngle = 0
  MakeFace = true
  Placement = pos=(-242.465,123.544,0) rot=(0,0,1;6.06485rad)
  Radius = 1
FEATURE [Part::Part2DObjectPython] Rectangle080  # Draft 2D object (typed FeaturePython)
  Area = 0
  ChamferSize = 0
  Columns = 1
  FilletRadius = 0
  Height = 8.42
  Length = 8.42
  MakeFace = false
  Placement = pos=(-247.407,112.594,0) rot=(0,0,1;2.73rad)
  Rows = 1
FEATURE [Part::Part2DObjectPython] Circle080  # Draft 2D object (typed FeaturePython)
  Area = 0
  FirstAngle = 0
  LastAngle = 0
  MakeFace = false
  Placement = pos=(-249.092,108.736,0) rot=(0,0,1;2.73rad)
  Radius = 1
FEATURE [Part::Part2DObjectPython] Rectangle081  # Draft 2D object (typed FeaturePython)
  Area = 0
  ChamferSize = 0
  Columns = 1
  FilletRadius = 0
  Height = 6
  Length = 6
  MakeFace = false
  Placement = pos=(-255.95,107.42,0) rot=(0,0,1;0rad)
  Rows = 1
FEATURE [Part::Part2DObjectPython] Circle081  # Draft 2D object (typed FeaturePython)
  Area = 3.14159
  FirstAngle = 0
  LastAngle = 0
  MakeFace = true
  Placement = pos=(-248.95,110.42,0) rot=(0,0,1;0rad)
  Radius = 1
FEATURE [Part::Part2DObjectPython] Rectangle082  # Draft 2D object (typed FeaturePython)
  Area = 0
  ChamferSize = 0
  Columns = 1
  FilletRadius = 0
  Height = 8.42
  Length = 8.42
  MakeFace = false
  Placement = pos=(-253.318,98.5709,0) rot=(0,0,1;2.78599rad)
  Rows = 1
FEATURE [Part::Part2DObjectPython] Circle082  # Draft 2D object (typed FeaturePython)
  Area = 0
  FirstAngle = 0
  LastAngle = 0
  MakeFace = false
  Placement = pos=(-254.783,94.6243,0) rot=(0,0,1;2.78599rad)
  Radius = 1
FEATURE [Part::Part2DObjectPython] Rectangle083  # Draft 2D object (typed FeaturePython)
  Area = 0
  ChamferSize = 0
  Columns = 1
  FilletRadius = 0
  Height = 6
  Length = 6
  MakeFace = false
  Placement = pos=(-261.73,93.09,0) rot=(0,0,1;0rad)
  Rows = 1
FEATURE [Part::Part2DObjectPython] Circle083  # Draft 2D object (typed FeaturePython)
  Area = 3.14159
  FirstAngle = 0
  LastAngle = 0
  MakeFace = true
  Placement = pos=(-254.73,96.09,0) rot=(0,0,1;0rad)
  Radius = 1
FEATURE [Part::Part2DObjectPython] Rectangle084  # Draft 2D object (typed FeaturePython)
  Area = 0
  ChamferSize = 0
  Columns = 1
  FilletRadius = 0
  Height = 8.42
  Length = 8.42
  MakeFace = false
  Placement = pos=(-267.255,49.5968,0) rot=(0,0,1;2.97359rad)
  Rows = 1
FEATURE [Part::Part2DObjectPython] Circle084  # Draft 2D object (typed FeaturePython)
  Area = 0
  FirstAngle = 0
  LastAngle = 0
  MakeFace = false
  Placement = pos=(-267.959,45.446,0) rot=(0,0,1;2.97359rad)
  Radius = 1
FEATURE [Part::Part2DObjectPython] Rectangle085  # Draft 2D object (typed FeaturePython)
  Area = 0
  ChamferSize = 0
  Columns = 1
  FilletRadius = 0
  Height = 6
  Length = 6
  MakeFace = false
  Placement = pos=(-275.11,43.15,0) rot=(0,0,1;0rad)
  Rows = 1
FEATURE [App::FeaturePython] Text012  # WARN: FeaturePython — macro-defined, semantics opaque (R4)
  Placement = pos=(-270.79,53.3517,0) rot=(0,0,-1;1.59733rad)
  Text = 0
FEATURE [App::FeaturePython] Text013  # WARN: FeaturePython — macro-defined, semantics opaque (R4)
  Placement = pos=(-268.047,-49.5386,0) rot=(0,0,1;5.7657rad)
  Text = 12
FEATURE [Part::Part2DObjectPython] Circle085  # Draft 2D object (typed FeaturePython)
  Area = 3.14159
  FirstAngle = 0
  LastAngle = 0
  MakeFace = true
  Placement = pos=(-268.11,46.15,0) rot=(0,0,1;0rad)
  Radius = 1
FEATURE [Part::Part2DObjectPython] Rectangle086  # Draft 2D object (typed FeaturePython)
  Area = 0
  ChamferSize = 0
  Columns = 1
  FilletRadius = 0
  Height = 8.42
  Length = 8.42
  MakeFace = false
  Placement = pos=(-269.616,34.563,0) rot=(0,0,1;3.02958rad)
  Rows = 1
FEATURE [Part::Part2DObjectPython] Circle086  # Draft 2D object (typed FeaturePython)
  Area = 0
  FirstAngle = 0
  LastAngle = 0
  MakeFace = false
  Placement = pos=(-270.086,30.3794,0) rot=(0,0,1;3.02958rad)
  Radius = 1
FEATURE [Part::Part2DObjectPython] Rectangle087  # Draft 2D object (typed FeaturePython)
  Area = 0
  ChamferSize = 0
  Columns = 1
  FilletRadius = 0
  Height = 6
  Length = 6
  MakeFace = false
  Placement = pos=(-277.27,27.85,0) rot=(0,0,1;0rad)
  Rows = 1
FEATURE [Part::Part2DObjectPython] Circle087  # Draft 2D object (typed FeaturePython)
  Area = 3.14159
  FirstAngle = 0
  LastAngle = 0
  MakeFace = true
  Placement = pos=(-270.27,30.85,0) rot=(0,0,1;0rad)
  Radius = 1
FEATURE [Part::Part2DObjectPython] Rectangle088  # Draft 2D object (typed FeaturePython)
  Area = 0
  ChamferSize = 0
  Columns = 1
  FilletRadius = 0
  Height = 8.42
  Length = 8.42
  MakeFace = false
  Placement = pos=(-271.131,19.4177,0) rot=(0,0,1;3.08559rad)
  Rows = 1
FEATURE [Part::Part2DObjectPython] Circle088  # Draft 2D object (typed FeaturePython)
  Area = 0
  FirstAngle = 0
  LastAngle = 0
  MakeFace = false
  Placement = pos=(-271.367,15.2143,0) rot=(0,0,1;3.08559rad)
  Radius = 1
FEATURE [Part::Part2DObjectPython] Rectangle089  # Draft 2D object (typed FeaturePython)
  Area = 0
  ChamferSize = 0
  Columns = 1
  FilletRadius = 0
  Height = 6
  Length = 6
  MakeFace = false
  Placement = pos=(-278.57,12.45,0) rot=(0,0,1;0rad)
  Rows = 1
FEATURE [Part::Part2DObjectPython] Circle089  # Draft 2D object (typed FeaturePython)
  Area = 3.14159
  FirstAngle = 0
  LastAngle = 0
  MakeFace = true
  Placement = pos=(-271.57,15.45,0) rot=(0,0,1;0rad)
  Radius = 1
FEATURE [Part::Part2DObjectPython] Rectangle090  # Draft 2D object (typed FeaturePython)
  Area = 0
  ChamferSize = 0
  Columns = 1
  FilletRadius = 0
  Height = 8.42
  Length = 8.42
  MakeFace = false
  Placement = pos=(-271.79,4.21,0) rot=(0,0,1;3.14159rad)
  Rows = 1
FEATURE [Part::Part2DObjectPython] Circle090  # Draft 2D object (typed FeaturePython)
  Area = 0
  FirstAngle = 0
  LastAngle = 0
  MakeFace = false
  Placement = pos=(-271.79,-5e-16,0) rot=(0,0,1;3.14159rad)
  Radius = 1
FEATURE [Part::Part2DObjectPython] Rectangle091  # Draft 2D object (typed FeaturePython)
  Area = 0
  ChamferSize = 0
  Columns = 1
  FilletRadius = 0
  Height = 6
  Length = 6
  MakeFace = false
  Placement = pos=(-272.368,-2.19273,0) rot=(0,0,1;1.81305rad)
  Rows = 1
FEATURE [Part::Part2DObjectPython] Circle091  # Draft 2D object (typed FeaturePython)
  Area = 3.14159
  FirstAngle = 0
  LastAngle = 0
  MakeFace = true
  Placement = pos=(-276.96,3.8832,0) rot=(0,0,1;1.81305rad)
  Radius = 1
FEATURE [Part::Part2DObjectPython] Rectangle092  # Draft 2D object (typed FeaturePython)
  Area = 0
  ChamferSize = 0
  Columns = 1
  FilletRadius = 0
  Height = 8.42
  Length = 8.42
  MakeFace = false
  Placement = pos=(-271.602,-11.0109,0) rot=(0,0,1;3.1976rad)
  Rows = 1
FEATURE [Part::Part2DObjectPython] Circle092  # Draft 2D object (typed FeaturePython)
  Area = 0
  FirstAngle = 0
  LastAngle = 0
  MakeFace = false
  Placement = pos=(-271.367,-15.2143,0) rot=(0,0,1;3.1976rad)
  Radius = 1
FEATURE [Part::Part2DObjectPython] Rectangle093  # Draft 2D object (typed FeaturePython)
  Area = 0
  ChamferSize = 0
  Columns = 1
  FilletRadius = 0
  Height = 6
  Length = 6
  MakeFace = false
  Placement = pos=(-271.699,-17.1865,0) rot=(0,0,1;1.93452rad)
  Rows = 1
FEATURE [Part::Part2DObjectPython] Circle093  # Draft 2D object (typed FeaturePython)
  Area = 3.14159
  FirstAngle = 0
  LastAngle = 0
  MakeFace = true
  Placement = pos=(-276.993,-11.7117,0) rot=(0,0,1;1.93452rad)
  Radius = 1
FEATURE [Part::Part2DObjectPython] Rectangle094  # Draft 2D object (typed FeaturePython)
  Area = 0
  ChamferSize = 0
  Columns = 1
  FilletRadius = 0
  Height = 8.42
  Length = 8.42
  MakeFace = false
  Placement = pos=(-270.557,-26.1958,0) rot=(0,0,1;3.2536rad)
  Rows = 1
FEATURE [Part::Part2DObjectPython] Circle094  # Draft 2D object (typed FeaturePython)
  Area = 0
  FirstAngle = 0
  LastAngle = 0
  MakeFace = false
  Placement = pos=(-270.086,-30.3794,0) rot=(0,0,1;3.2536rad)
  Radius = 1
FEATURE [Part::Part2DObjectPython] Rectangle095  # Draft 2D object (typed FeaturePython)
  Area = 0
  ChamferSize = 0
  Columns = 1
  FilletRadius = 0
  Height = 6
  Length = 6
  MakeFace = false
  Placement = pos=(-270.258,-32.2306,0) rot=(0,0,1;2.02476rad)
  Rows = 1
FEATURE [Part::Part2DObjectPython] Circle095  # Draft 2D object (typed FeaturePython)
  Area = 3.14159
  FirstAngle = 0
  LastAngle = 0
  MakeFace = true
  Placement = pos=(-276.024,-27.2551,0) rot=(0,0,1;2.02476rad)
  Radius = 1
FEATURE [Part::Part2DObjectPython] Rectangle096  # Draft 2D object (typed FeaturePython)
  Area = 0
  ChamferSize = 0
  Columns = 1
  FilletRadius = 0
  Height = 8.42
  Length = 8.42
  MakeFace = false
  Placement = pos=(-268.663,-41.2953,0) rot=(0,0,1;3.30959rad)
  Rows = 1
FEATURE [Part::Part2DObjectPython] Circle096  # Draft 2D object (typed FeaturePython)
  Area = 0
  FirstAngle = 0
  LastAngle = 0
  MakeFace = false
  Placement = pos=(-267.959,-45.446,0) rot=(0,0,1;3.30959rad)
  Radius = 1
FEATURE [Part::Part2DObjectPython] Rectangle097  # Draft 2D object (typed FeaturePython)
  Area = 0
  ChamferSize = 0
  Columns = 1
  FilletRadius = 0
  Height = 6
  Length = 6
  MakeFace = false
  Placement = pos=(-268.022,-47.2859,0) rot=(0,0,1;2.08514rad)
  Rows = 1
FEATURE [Part::Part2DObjectPython] Circle097  # Draft 2D object (typed FeaturePython)
  Area = 3.14159
  FirstAngle = 0
  LastAngle = 0
  MakeFace = true
  Placement = pos=(-274.078,-42.6675,0) rot=(0,0,1;2.08514rad)
  Radius = 1
FEATURE [Part::Part2DObjectPython] Rectangle098  # Draft 2D object (typed FeaturePython)
  Area = 0
  ChamferSize = 0
  Columns = 1
  FilletRadius = 0
  Height = 8.42
  Length = 8.42
  MakeFace = false
  Placement = pos=(-256.249,-90.6777,0) rot=(0,0,1;3.4972rad)
  Rows = 1
FEATURE [Part::Part2DObjectPython] Circle098  # Draft 2D object (typed FeaturePython)
  Area = 0
  FirstAngle = 0
  LastAngle = 0
  MakeFace = false
  Placement = pos=(-254.783,-94.6243,0) rot=(0,0,1;3.4972rad)
  Radius = 1
FEATURE [Part::Part2DObjectPython] Rectangle099  # Draft 2D object (typed FeaturePython)
  Area = 0
  ChamferSize = 0
  Columns = 1
  FilletRadius = 0
  Height = 6
  Length = 6
  MakeFace = false
  Placement = pos=(-254.646,-97.2388,0) rot=(0,0,1;2.082rad)
  Rows = 1
FEATURE [App::FeaturePython] Text014  # WARN: FeaturePython — macro-defined, semantics opaque (R4)
  Placement = pos=(-261.188,-89.1931,0) rot=(0,0,-1;1.07373rad)
  Text = 0
FEATURE [App::FeaturePython] Text015  # WARN: FeaturePython — macro-defined, semantics opaque (R4)
  Placement = pos=(-207.363,-176.926,0) rot=(0,0,-1;6.27708rad)
  Text = 1
FEATURE [Part::Part2DObjectPython] Circle099  # Draft 2D object (typed FeaturePython)
  Area = 3.14159
  FirstAngle = 0
  LastAngle = 0
  MakeFace = true
  Placement = pos=(-260.687,-92.6014,0) rot=(0,0,1;2.082rad)
  Radius = 1
FEATURE [Part::Part2DObjectPython] Rectangle100  # Draft 2D object (typed FeaturePython)
  Area = 0
  ChamferSize = 0
  Columns = 1
  FilletRadius = 0
  Height = 8.42
  Length = 8.42
  MakeFace = false
  Placement = pos=(-250.776,-104.877,0) rot=(0,0,1;3.55319rad)
  Rows = 1
FEATURE [Part::Part2DObjectPython] Circle100  # Draft 2D object (typed FeaturePython)
  Area = 0
  FirstAngle = 0
  LastAngle = 0
  MakeFace = false
  Placement = pos=(-249.092,-108.736,0) rot=(0,0,1;3.55319rad)
  Radius = 1
FEATURE [Part::Part2DObjectPython] Rectangle101  # Draft 2D object (typed FeaturePython)
  Area = 0
  ChamferSize = 0
  Columns = 1
  FilletRadius = 0
  Height = 6
  Length = 6
  MakeFace = false
  Placement = pos=(-248.887,-111.641,0) rot=(0,0,1;2.06438rad)
  Rows = 1
FEATURE [Part::Part2DObjectPython] Circle101  # Draft 2D object (typed FeaturePython)
  Area = 3.14159
  FirstAngle = 0
  LastAngle = 0
  MakeFace = true
  Placement = pos=(-254.845,-106.897,0) rot=(0,0,1;2.06438rad)
  Radius = 1
FEATURE [Part::Part2DObjectPython] Rectangle102  # Draft 2D object (typed FeaturePython)
  Area = 0
  ChamferSize = 0
  Columns = 1
  FilletRadius = 0
  Height = 8.42
  Length = 8.42
  MakeFace = false
  Placement = pos=(-244.51,-118.754,0) rot=(0,0,1;3.60921rad)
  Rows = 1
FEATURE [Part::Part2DObjectPython] Circle102  # Draft 2D object (typed FeaturePython)
  Area = 0
  FirstAngle = 0
  LastAngle = 0
  MakeFace = false
  Placement = pos=(-242.612,-122.512,0) rot=(0,0,1;3.60921rad)
  Radius = 1
FEATURE [Part::Part2DObjectPython] Rectangle103  # Draft 2D object (typed FeaturePython)
  Area = 0
  ChamferSize = 0
  Columns = 1
  FilletRadius = 0
  Height = 6
  Length = 6
  MakeFace = false
  Placement = pos=(-242.318,-125.667,0) rot=(0,0,1;2.05547rad)
  Rows = 1
FEATURE [Part::Part2DObjectPython] Circle103  # Draft 2D object (typed FeaturePython)
  Area = 3.14159
  FirstAngle = 0
  LastAngle = 0
  MakeFace = true
  Placement = pos=(-248.234,-120.871,0) rot=(0,0,1;2.05547rad)
  Radius = 1
FEATURE [Part::Part2DObjectPython] Rectangle104  # Draft 2D object (typed FeaturePython)
  Area = 0
  ChamferSize = 0
  Columns = 1
  FilletRadius = 0
  Height = 8.42
  Length = 8.42
  MakeFace = false
  Placement = pos=(-237.479,-132.249,0) rot=(0,0,1;3.6652rad)
  Rows = 1
FEATURE [Part::Part2DObjectPython] Circle104  # Draft 2D object (typed FeaturePython)
  Area = 0
  FirstAngle = 0
  LastAngle = 0
  MakeFace = false
  Placement = pos=(-235.374,-135.895,0) rot=(0,0,1;3.6652rad)
  Radius = 1
FEATURE [Part::Part2DObjectPython] Rectangle105  # Draft 2D object (typed FeaturePython)
  Area = 0
  ChamferSize = 0
  Columns = 1
  FilletRadius = 0
  Height = 6
  Length = 6
  MakeFace = false
  Placement = pos=(-235.006,-139.374,0) rot=(0,0,1;2.0265rad)
  Rows = 1
FEATURE [Part::Part2DObjectPython] Circle105  # Draft 2D object (typed FeaturePython)
  Area = 3.14159
  FirstAngle = 0
  LastAngle = 0
  MakeFace = true
  Placement = pos=(-240.78,-134.408,0) rot=(0,0,1;2.0265rad)
  Radius = 1
FEATURE [Part::Part2DObjectPython] Rectangle106  # Draft 2D object (typed FeaturePython)
  Area = 0
  ChamferSize = 0
  Columns = 1
  FilletRadius = 0
  Height = 8.42
  Length = 8.42
  MakeFace = false
  Placement = pos=(-229.703,-145.332,0) rot=(0,0,1;3.72119rad)
  Rows = 1
FEATURE [Part::Part2DObjectPython] Circle106  # Draft 2D object (typed FeaturePython)
  Area = 0
  FirstAngle = 0
  LastAngle = 0
  MakeFace = false
  Placement = pos=(-227.398,-148.854,0) rot=(0,0,1;3.72119rad)
  Radius = 1
FEATURE [Part::Part2DObjectPython] Rectangle107  # Draft 2D object (typed FeaturePython)
  Area = 0
  ChamferSize = 0
  Columns = 1
  FilletRadius = 0
  Height = 6
  Length = 6
  MakeFace = false
  Placement = pos=(-229.308,-155.084,0) rot=(0,0,1;1.17513rad)
  Rows = 1
FEATURE [Part::Part2DObjectPython] Circle107  # Draft 2D object (typed FeaturePython)
  Area = 3.14159
  FirstAngle = 0
  LastAngle = 0
  MakeFace = true
  Placement = pos=(-229.378,-147.469,0) rot=(0,0,1;1.17513rad)
  Radius = 1
FEATURE [Part::Part2DObjectPython] Rectangle108  # Draft 2D object (typed FeaturePython)
  Area = 0
  ChamferSize = 0
  Columns = 1
  FilletRadius = 0
  Height = 8.42
  Length = 8.42
  MakeFace = false
  Placement = pos=(-221.211,-157.963,0) rot=(0,0,1;3.77719rad)
  Rows = 1
FEATURE [Part::Part2DObjectPython] Circle108  # Draft 2D object (typed FeaturePython)
  Area = 0
  FirstAngle = 0
  LastAngle = 0
  MakeFace = false
  Placement = pos=(-218.712,-161.351,0) rot=(0,0,1;3.77719rad)
  Radius = 1
FEATURE [Part::Part2DObjectPython] Rectangle109  # Draft 2D object (typed FeaturePython)
  Area = 0
  ChamferSize = 0
  Columns = 1
  FilletRadius = 0
  Height = 6
  Length = 6
  MakeFace = false
  Placement = pos=(-225.094,-166.856,0) rot=(0,0,1;0.00192rad)
  Rows = 1
FEATURE [Part::Part2DObjectPython] Circle109  # Draft 2D object (typed FeaturePython)
  Area = 3.14159
  FirstAngle = 0
  LastAngle = 0
  MakeFace = true
  Placement = pos=(-218.1,-163.842,0) rot=(0,0,1;0.00192rad)
  Radius = 1
FEATURE [Part::Part2DObjectPython] Rectangle110  # Draft 2D object (typed FeaturePython)
  Area = 0
  ChamferSize = 0
  Columns = 1
  FilletRadius = 0
  Height = 8.42
  Length = 8.42
  MakeFace = false
  Placement = pos=(-212.022,-170.092,0) rot=(0,0,1;3.83319rad)
  Rows = 1
FEATURE [Part::Part2DObjectPython] Circle110  # Draft 2D object (typed FeaturePython)
  Area = 0
  FirstAngle = 0
  LastAngle = 0
  MakeFace = false
  Placement = pos=(-209.337,-173.335,0) rot=(0,0,1;3.83319rad)
  Radius = 1
FEATURE [Part::Part2DObjectPython] Rectangle111  # Draft 2D object (typed FeaturePython)
  Area = 0
  ChamferSize = 0
  Columns = 1
  FilletRadius = 0
  Height = 6
  Length = 6
  MakeFace = false
  Placement = pos=(-215.58,-179.02,0) rot=(0,0,1;0rad)
  Rows = 1
FEATURE [Part::Part2DObjectPython] Circle111  # Draft 2D object (typed FeaturePython)
  Area = 3.14159
  FirstAngle = 0
  LastAngle = 0
  MakeFace = true
  Placement = pos=(-208.58,-176.02,0) rot=(0,0,1;0rad)
  Radius = 1
FEATURE [Part::Part2DObjectPython] Rectangle112  # Draft 2D object (typed FeaturePython)
  Area = 0
  ChamferSize = 0
  Columns = 1
  FilletRadius = 0
  Height = 8.42
  Length = 8.42
  MakeFace = false
  Placement = pos=(-176.578,-206.652,0) rot=(0,0,1;4.0208rad)
  Rows = 1
FEATURE [Part::Part2DObjectPython] Circle112  # Draft 2D object (typed FeaturePython)
  Area = 0
  FirstAngle = 0
  LastAngle = 0
  MakeFace = false
  Placement = pos=(-173.335,-209.337,0) rot=(0,0,1;4.0208rad)
  Radius = 1
FEATURE [Part::Part2DObjectPython] Rectangle113  # Draft 2D object (typed FeaturePython)
  Area = 0
  ChamferSize = 0
  Columns = 1
  FilletRadius = 0
  Height = 6
  Length = 6
  MakeFace = false
  Placement = pos=(-179.02,-215.58,0) rot=(0,0,1;0rad)
  Rows = 1
FEATURE [App::FeaturePython] Text016  # WARN: FeaturePython — macro-defined, semantics opaque (R4)
  Placement = pos=(-181.597,-207.836,0) rot=(0,0,-1;0.550128rad)
  Text = 0
FEATURE [App::FeaturePython] Text017  # WARN: FeaturePython — macro-defined, semantics opaque (R4)
  Placement = pos=(-91.1209,-256.902,0) rot=(0,0,-1;5.75348rad)
  Text = 2
FEATURE [Part::Part2DObjectPython] Circle113  # Draft 2D object (typed FeaturePython)
  Area = 3.14159
  FirstAngle = 0
  LastAngle = 0
  MakeFace = true
  Placement = pos=(-172.02,-212.58,0) rot=(0,0,1;0rad)
  Radius = 1
FEATURE [Part::Part2DObjectPython] Rectangle114  # Draft 2D object (typed FeaturePython)
  Area = 0
  ChamferSize = 0
  Columns = 1
  FilletRadius = 0
  Height = 8.42
  Length = 8.42
  MakeFace = false
  Placement = pos=(-164.739,-216.213,0) rot=(0,0,1;4.07679rad)
  Rows = 1
FEATURE [Part::Part2DObjectPython] Circle114  # Draft 2D object (typed FeaturePython)
  Area = 0
  FirstAngle = 0
  LastAngle = 0
  MakeFace = false
  Placement = pos=(-161.351,-218.712,0) rot=(0,0,1;4.07679rad)
  Radius = 1
FEATURE [Part::Part2DObjectPython] Rectangle115  # Draft 2D object (typed FeaturePython)
  Area = 0
  ChamferSize = 0
  Columns = 1
  FilletRadius = 0
  Height = 6
  Length = 6
  MakeFace = false
  Placement = pos=(-166.85,-225.1,0) rot=(0,0,1;0rad)
  Rows = 1
FEATURE [Part::Part2DObjectPython] Circle115  # Draft 2D object (typed FeaturePython)
  Area = 3.14159
  FirstAngle = 0
  LastAngle = 0
  MakeFace = true
  Placement = pos=(-159.85,-222.1,0) rot=(0,0,1;0rad)
  Radius = 1
FEATURE [Part::Part2DObjectPython] Rectangle116  # Draft 2D object (typed FeaturePython)
  Area = 0
  ChamferSize = 0
  Columns = 1
  FilletRadius = 0
  Height = 8.42
  Length = 8.42
  MakeFace = false
  Placement = pos=(-152.377,-225.092,0) rot=(0,0,1;4.13279rad)
  Rows = 1
FEATURE [Part::Part2DObjectPython] Circle116  # Draft 2D object (typed FeaturePython)
  Area = 0
  FirstAngle = 0
  LastAngle = 0
  MakeFace = false
  Placement = pos=(-148.854,-227.398,0) rot=(0,0,1;4.13279rad)
  Radius = 1
FEATURE [Part::Part2DObjectPython] Rectangle117  # Draft 2D object (typed FeaturePython)
  Area = 0
  ChamferSize = 0
  Columns = 1
  FilletRadius = 0
  Height = 6
  Length = 6
  MakeFace = false
  Placement = pos=(-153.761,-234.272,0) rot=(0,0,1;0.125489rad)
  Rows = 1
FEATURE [Part::Part2DObjectPython] Circle117  # Draft 2D object (typed FeaturePython)
  Area = 3.14159
  FirstAngle = 0
  LastAngle = 0
  MakeFace = true
  Placement = pos=(-147.191,-230.419,0) rot=(0,0,1;0.125489rad)
  Radius = 1
FEATURE [Part::Part2DObjectPython] Rectangle118  # Draft 2D object (typed FeaturePython)
  Area = 0
  ChamferSize = 0
  Columns = 1
  FilletRadius = 0
  Height = 8.42
  Length = 8.42
  MakeFace = false
  Placement = pos=(-139.541,-233.269,0) rot=(0,0,1;4.18879rad)
  Rows = 1
FEATURE [Part::Part2DObjectPython] Circle118  # Draft 2D object (typed FeaturePython)
  Area = 0
  FirstAngle = 0
  LastAngle = 0
  MakeFace = false
  Placement = pos=(-135.895,-235.374,0) rot=(0,0,1;4.18879rad)
  Radius = 1
FEATURE [Part::Part2DObjectPython] Rectangle119  # Draft 2D object (typed FeaturePython)
  Area = 0
  ChamferSize = 0
  Columns = 1
  FilletRadius = 0
  Height = 6
  Length = 6
  MakeFace = false
  Placement = pos=(-140.093,-242.71,0) rot=(0,0,1;0.269479rad)
  Rows = 1
FEATURE [Part::Part2DObjectPython] Circle119  # Draft 2D object (typed FeaturePython)
  Area = 3.14159
  FirstAngle = 0
  LastAngle = 0
  MakeFace = true
  Placement = pos=(-134.144,-237.955,0) rot=(0,0,1;0.269479rad)
  Radius = 1
FEATURE [Part::Part2DObjectPython] Rectangle120  # Draft 2D object (typed FeaturePython)
  Area = 0
  ChamferSize = 0
  Columns = 1
  FilletRadius = 0
  Height = 8.42
  Length = 8.42
  MakeFace = false
  Placement = pos=(-126.27,-240.714,0) rot=(0,0,1;4.24477rad)
  Rows = 1
FEATURE [Part::Part2DObjectPython] Circle120  # Draft 2D object (typed FeaturePython)
  Area = 0
  FirstAngle = 0
  LastAngle = 0
  MakeFace = false
  Placement = pos=(-122.512,-242.612,0) rot=(0,0,1;4.24477rad)
  Radius = 1
FEATURE [Part::Part2DObjectPython] Rectangle121  # Draft 2D object (typed FeaturePython)
  Area = 0
  ChamferSize = 0
  Columns = 1
  FilletRadius = 0
  Height = 6
  Length = 6
  MakeFace = false
  Placement = pos=(-125.95,-250.323,0) rot=(0,0,1;0.413818rad)
  Rows = 1
FEATURE [Part::Part2DObjectPython] Circle121  # Draft 2D object (typed FeaturePython)
  Area = 3.14159
  FirstAngle = 0
  LastAngle = 0
  MakeFace = true
  Placement = pos=(-120.748,-244.762,0) rot=(0,0,1;0.413818rad)
  Radius = 1
FEATURE [Part::Part2DObjectPython] Rectangle122  # Draft 2D object (typed FeaturePython)
  Area = 0
  ChamferSize = 0
  Columns = 1
  FilletRadius = 0
  Height = 8.42
  Length = 8.42
  MakeFace = false
  Placement = pos=(-112.594,-247.407,0) rot=(0,0,1;4.30079rad)
  Rows = 1
FEATURE [Part::Part2DObjectPython] Circle122  # Draft 2D object (typed FeaturePython)
  Area = 0
  FirstAngle = 0
  LastAngle = 0
  MakeFace = false
  Placement = pos=(-108.736,-249.092,0) rot=(0,0,1;4.30079rad)
  Radius = 1
FEATURE [Part::Part2DObjectPython] Rectangle123  # Draft 2D object (typed FeaturePython)
  Area = 0
  ChamferSize = 0
  Columns = 1
  FilletRadius = 0
  Height = 6
  Length = 6
  MakeFace = false
  Placement = pos=(-111.377,-257.083,0) rot=(0,0,1;0.557982rad)
  Rows = 1
FEATURE [Part::Part2DObjectPython] Circle123  # Draft 2D object (typed FeaturePython)
  Area = 3.14159
  FirstAngle = 0
  LastAngle = 0
  MakeFace = true
  Placement = pos=(-107.027,-250.832,0) rot=(0,0,1;0.557982rad)
  Radius = 1
FEATURE [Part::Part2DObjectPython] Rectangle124  # Draft 2D object (typed FeaturePython)
  Area = 0
  ChamferSize = 0
  Columns = 1
  FilletRadius = 0
  Height = 8.42
  Length = 8.42
  MakeFace = false
  Placement = pos=(-98.5709,-253.318,0) rot=(0,0,1;4.35679rad)
  Rows = 1
FEATURE [Part::Part2DObjectPython] Circle124  # Draft 2D object (typed FeaturePython)
  Area = 0
  FirstAngle = 0
  LastAngle = 0
  MakeFace = false
  Placement = pos=(-94.6243,-254.783,0) rot=(0,0,1;4.35679rad)
  Radius = 1
FEATURE [Part::Part2DObjectPython] Rectangle125  # Draft 2D object (typed FeaturePython)
  Area = 0
  ChamferSize = 0
  Columns = 1
  FilletRadius = 0
  Height = 6
  Length = 6
  MakeFace = false
  Placement = pos=(-96.445,-262.958,0) rot=(0,0,1;0.701622rad)
  Rows = 1
FEATURE [Part::Part2DObjectPython] Circle125  # Draft 2D object (typed FeaturePython)
  Area = 3.14159
  FirstAngle = 0
  LastAngle = 0
  MakeFace = true
  Placement = pos=(-93.0348,-256.148,0) rot=(0,0,1;0.701622rad)
  Radius = 1
FEATURE [Part::Part2DObjectPython] Rectangle126  # Draft 2D object (typed FeaturePython)
  Area = 0
  ChamferSize = 0
  Columns = 1
  FilletRadius = 0
  Height = 8.42
  Length = 8.42
  MakeFace = false
  Placement = pos=(-49.5968,-267.255,0) rot=(0,0,1;4.54439rad)
  Rows = 1
FEATURE [Part::Part2DObjectPython] Circle126  # Draft 2D object (typed FeaturePython)
  Area = 0
  FirstAngle = 0
  LastAngle = 0
  MakeFace = false
  Placement = pos=(-45.446,-267.959,0) rot=(0,0,1;4.54439rad)
  Radius = 1
FEATURE [Part::Part2DObjectPython] Rectangle127  # Draft 2D object (typed FeaturePython)
  Area = 0
  ChamferSize = 0
  Columns = 1
  FilletRadius = 0
  Height = 6
  Length = 6
  MakeFace = false
  Placement = pos=(-44.495,-276.017,0) rot=(0,0,1;1.18613rad)
  Rows = 1
FEATURE [App::FeaturePython] Text018  # WARN: FeaturePython — macro-defined, semantics opaque (R4)
  Placement = pos=(-53.3517,-270.79,0) rot=(0,0,1;6.25666rad)
  Text = 0
FEATURE [App::FeaturePython] Text019  # WARN: FeaturePython — macro-defined, semantics opaque (R4)
  Placement = pos=(49.5386,-268.047,0) rot=(0,0,1;1.05331rad)
  Text = 3
FEATURE [Part::Part2DObjectPython] Circle127  # Draft 2D object (typed FeaturePython)
  Area = 3.14159
  FirstAngle = 0
  LastAngle = 0
  MakeFace = true
  Placement = pos=(-44.649,-268.402,0) rot=(0,0,1;1.18613rad)
  Radius = 1
FEATURE [Part::Part2DObjectPython] Rectangle128  # Draft 2D object (typed FeaturePython)
  Area = 0
  ChamferSize = 0
  Columns = 1
  FilletRadius = 0
  Height = 8.42
  Length = 8.42
  MakeFace = false
  Placement = pos=(-34.563,-269.616,0) rot=(0,0,1;4.60038rad)
  Rows = 1
FEATURE [Part::Part2DObjectPython] Circle128  # Draft 2D object (typed FeaturePython)
  Area = 0
  FirstAngle = 0
  LastAngle = 0
  MakeFace = false
  Placement = pos=(-30.3794,-270.086,0) rot=(0,0,1;4.60038rad)
  Radius = 1
FEATURE [Part::Part2DObjectPython] Rectangle129  # Draft 2D object (typed FeaturePython)
  Area = 0
  ChamferSize = 0
  Columns = 1
  FilletRadius = 0
  Height = 6
  Length = 6
  MakeFace = false
  Placement = pos=(-28.6459,-277.895,0) rot=(0,0,1;1.33169rad)
  Rows = 1
FEATURE [Part::Part2DObjectPython] Circle129  # Draft 2D object (typed FeaturePython)
  Area = 3.14159
  FirstAngle = 0
  LastAngle = 0
  MakeFace = true
  Placement = pos=(-29.9026,-270.384,0) rot=(0,0,1;1.33169rad)
  Radius = 1
FEATURE [Part::Part2DObjectPython] Rectangle130  # Draft 2D object (typed FeaturePython)
  Area = 0
  ChamferSize = 0
  Columns = 1
  FilletRadius = 0
  Height = 8.42
  Length = 8.42
  MakeFace = false
  Placement = pos=(-19.4177,-271.131,0) rot=(0,0,1;4.65638rad)
  Rows = 1
FEATURE [Part::Part2DObjectPython] Circle130  # Draft 2D object (typed FeaturePython)
  Area = 0
  FirstAngle = 0
  LastAngle = 0
  MakeFace = false
  Placement = pos=(-15.2143,-271.367,0) rot=(0,0,1;4.65638rad)
  Radius = 1
FEATURE [Part::Part2DObjectPython] Rectangle131  # Draft 2D object (typed FeaturePython)
  Area = 0
  ChamferSize = 0
  Columns = 1
  FilletRadius = 0
  Height = 6
  Length = 6
  MakeFace = false
  Placement = pos=(-18.45,-278.57,0) rot=(0,0,1;0rad)
  Rows = 1
FEATURE [Part::Part2DObjectPython] Circle131  # Draft 2D object (typed FeaturePython)
  Area = 3.14159
  FirstAngle = 0
  LastAngle = 0
  MakeFace = true
  Placement = pos=(-11.45,-275.57,0) rot=(0,0,1;0rad)
  Radius = 1
FEATURE [Part::Part2DObjectPython] Rectangle132  # Draft 2D object (typed FeaturePython)
  Area = 0
  ChamferSize = 0
  Columns = 1
  FilletRadius = 0
  Height = 8.42
  Length = 8.42
  MakeFace = false
  Placement = pos=(-4.21,-271.79,0) rot=(0,0,1;4.71239rad)
  Rows = 1
FEATURE [Part::Part2DObjectPython] Circle132  # Draft 2D object (typed FeaturePython)
  Area = 0
  FirstAngle = 0
  LastAngle = 0
  MakeFace = false
  Placement = pos=(0,-271.79,0) rot=(0,0,1;4.71239rad)
  Radius = 1
FEATURE [Part::Part2DObjectPython] Rectangle133  # Draft 2D object (typed FeaturePython)
  Area = 0
  ChamferSize = 0
  Columns = 1
  FilletRadius = 0
  Height = 6
  Length = 6
  MakeFace = false
  Placement = pos=(3.1687,-278.821,0) rot=(0,0,1;1.62874rad)
  Rows = 1
FEATURE [Part::Part2DObjectPython] Circle133  # Draft 2D object (typed FeaturePython)
  Area = 3.14159
  FirstAngle = 0
  LastAngle = 0
  MakeFace = true
  Placement = pos=(-0.23165,-272.007,0) rot=(0,0,1;1.62874rad)
  Radius = 1
FEATURE [Part::Part2DObjectPython] Rectangle134  # Draft 2D object (typed FeaturePython)
  Area = 0
  ChamferSize = 0
  Columns = 1
  FilletRadius = 0
  Height = 8.42
  Length = 8.42
  MakeFace = false
  Placement = pos=(11.0109,-271.602,0) rot=(0,0,1;4.7684rad)
  Rows = 1
FEATURE [Part::Part2DObjectPython] Circle134  # Draft 2D object (typed FeaturePython)
  Area = 0
  FirstAngle = 0
  LastAngle = 0
  MakeFace = false
  Placement = pos=(15.2143,-271.367,0) rot=(0,0,1;4.7684rad)
  Radius = 1
FEATURE [Part::Part2DObjectPython] Rectangle135  # Draft 2D object (typed FeaturePython)
  Area = 0
  ChamferSize = 0
  Columns = 1
  FilletRadius = 0
  Height = 6
  Length = 6
  MakeFace = false
  Placement = pos=(19.0033,-277.888,0) rot=(0,0,1;1.77814rad)
  Rows = 1
FEATURE [Part::Part2DObjectPython] Circle135  # Draft 2D object (typed FeaturePython)
  Area = 3.14159
  FirstAngle = 0
  LastAngle = 0
  MakeFace = true
  Placement = pos=(14.6265,-271.656,0) rot=(0,0,1;1.77814rad)
  Radius = 1
FEATURE [Part::Part2DObjectPython] Rectangle136  # Draft 2D object (typed FeaturePython)
  Area = 0
  ChamferSize = 0
  Columns = 1
  FilletRadius = 0
  Height = 8.42
  Length = 8.42
  MakeFace = false
  Placement = pos=(26.1958,-270.557,0) rot=(0,0,1;4.8244rad)
  Rows = 1
FEATURE [Part::Part2DObjectPython] Circle136  # Draft 2D object (typed FeaturePython)
  Area = 0
  FirstAngle = 0
  LastAngle = 0
  MakeFace = false
  Placement = pos=(30.3794,-270.086,0) rot=(0,0,1;4.8244rad)
  Radius = 1
FEATURE [Part::Part2DObjectPython] Rectangle137  # Draft 2D object (typed FeaturePython)
  Area = 0
  ChamferSize = 0
  Columns = 1
  FilletRadius = 0
  Height = 6
  Length = 6
  MakeFace = false
  Placement = pos=(34.7128,-276.025,0) rot=(0,0,1;1.92981rad)
  Rows = 1
FEATURE [Part::Part2DObjectPython] Circle137  # Draft 2D object (typed FeaturePython)
  Area = 3.14159
  FirstAngle = 0
  LastAngle = 0
  MakeFace = true
  Placement = pos=(29.4446,-270.525,0) rot=(0,0,1;1.92981rad)
  Radius = 1
FEATURE [Part::Part2DObjectPython] Rectangle138  # Draft 2D object (typed FeaturePython)
  Area = 0
  ChamferSize = 0
  Columns = 1
  FilletRadius = 0
  Height = 8.42
  Length = 8.42
  MakeFace = false
  Placement = pos=(41.2953,-268.663,0) rot=(0,0,1;4.88039rad)
  Rows = 1
FEATURE [Part::Part2DObjectPython] Circle138  # Draft 2D object (typed FeaturePython)
  Area = 0
  FirstAngle = 0
  LastAngle = 0
  MakeFace = false
  Placement = pos=(45.446,-267.959,0) rot=(0,0,1;4.88039rad)
  Radius = 1
FEATURE [Part::Part2DObjectPython] Rectangle139  # Draft 2D object (typed FeaturePython)
  Area = 0
  ChamferSize = 0
  Columns = 1
  FilletRadius = 0
  Height = 6
  Length = 6
  MakeFace = false
  Placement = pos=(50.2362,-273.252,0) rot=(0,0,1;2.08375rad)
  Rows = 1
FEATURE [Part::Part2DObjectPython] Circle139  # Draft 2D object (typed FeaturePython)
  Area = 3.14159
  FirstAngle = 0
  LastAngle = 0
  MakeFace = true
  Placement = pos=(44.187,-268.625,0) rot=(0,0,1;2.08375rad)
  Radius = 1
FEATURE [Part::Part2DObjectPython] Rectangle140  # Draft 2D object (typed FeaturePython)
  Area = 0
  ChamferSize = 0
  Columns = 1
  FilletRadius = 0
  Height = 8.42
  Length = 8.42
  MakeFace = false
  Placement = pos=(90.6777,-256.249,0) rot=(0,0,1;5.06799rad)
  Rows = 1
FEATURE [Part::Part2DObjectPython] Circle140  # Draft 2D object (typed FeaturePython)
  Area = 0
  FirstAngle = 0
  LastAngle = 0
  MakeFace = false
  Placement = pos=(94.6243,-254.783,0) rot=(0,0,1;5.06799rad)
  Radius = 1
FEATURE [Part::Part2DObjectPython] Rectangle141  # Draft 2D object (typed FeaturePython)
  Area = 0
  ChamferSize = 0
  Columns = 1
  FilletRadius = 0
  Height = 6
  Length = 6
  MakeFace = false
  Placement = pos=(100.186,-257.625,0) rot=(0,0,1;2.61957rad)
  Rows = 1
FEATURE [App::FeaturePython] Text020  # WARN: FeaturePython — macro-defined, semantics opaque (R4)
  Placement = pos=(89.1931,-261.188,0) rot=(0,0,-1;5.78612rad)
  Text = 0
FEATURE [App::FeaturePython] Text021  # WARN: FeaturePython — macro-defined, semantics opaque (R4)
  Placement = pos=(176.926,-207.363,0) rot=(0,0,1;1.57691rad)
  Text = 4
FEATURE [Part::Part2DObjectPython] Circle141  # Draft 2D object (typed FeaturePython)
  Area = 3.14159
  FirstAngle = 0
  LastAngle = 0
  MakeFace = true
  Placement = pos=(92.6228,-256.735,0) rot=(0,0,1;2.61957rad)
  Radius = 1
FEATURE [Part::Part2DObjectPython] Rectangle142  # Draft 2D object (typed FeaturePython)
  Area = 0
  ChamferSize = 0
  Columns = 1
  FilletRadius = 0
  Height = 8.42
  Length = 8.42
  MakeFace = false
  Placement = pos=(104.877,-250.776,0) rot=(0,0,1;5.12398rad)
  Rows = 1
FEATURE [Part::Part2DObjectPython] Circle142  # Draft 2D object (typed FeaturePython)
  Area = 0
  FirstAngle = 0
  LastAngle = 0
  MakeFace = false
  Placement = pos=(108.736,-249.092,0) rot=(0,0,1;5.12398rad)
  Radius = 1
FEATURE [Part::Part2DObjectPython] Rectangle143  # Draft 2D object (typed FeaturePython)
  Area = 0
  ChamferSize = 0
  Columns = 1
  FilletRadius = 0
  Height = 6
  Length = 6
  MakeFace = false
  Placement = pos=(114.274,-251.175,0) rot=(0,0,1;2.78781rad)
  Rows = 1
FEATURE [Part::Part2DObjectPython] Circle143  # Draft 2D object (typed FeaturePython)
  Area = 3.14159
  FirstAngle = 0
  LastAngle = 0
  MakeFace = true
  Placement = pos=(106.668,-251.564,0) rot=(0,0,1;2.78781rad)
  Radius = 1
FEATURE [Part::Part2DObjectPython] Rectangle144  # Draft 2D object (typed FeaturePython)
  Area = 0
  ChamferSize = 0
  Columns = 1
  FilletRadius = 0
  Height = 8.42
  Length = 8.42
  MakeFace = false
  Placement = pos=(118.754,-244.51,0) rot=(0,0,1;5.18001rad)
  Rows = 1
FEATURE [Part::Part2DObjectPython] Circle144  # Draft 2D object (typed FeaturePython)
  Area = 0
  FirstAngle = 0
  LastAngle = 0
  MakeFace = false
  Placement = pos=(122.512,-242.612,0) rot=(0,0,1;5.18001rad)
  Radius = 1
FEATURE [Part::Part2DObjectPython] Rectangle145  # Draft 2D object (typed FeaturePython)
  Area = 0
  ChamferSize = 0
  Columns = 1
  FilletRadius = 0
  Height = 6
  Length = 6
  MakeFace = false
  Placement = pos=(127.902,-243.961,0) rot=(0,0,1;2.96008rad)
  Rows = 1
FEATURE [Part::Part2DObjectPython] Circle145  # Draft 2D object (typed FeaturePython)
  Area = 3.14159
  FirstAngle = 0
  LastAngle = 0
  MakeFace = true
  Placement = pos=(120.476,-245.648,0) rot=(0,0,1;2.96008rad)
  Radius = 1
FEATURE [Part::Part2DObjectPython] Rectangle146  # Draft 2D object (typed FeaturePython)
  Area = 0
  ChamferSize = 0
  Columns = 1
  FilletRadius = 0
  Height = 8.42
  Length = 8.42
  MakeFace = false
  Placement = pos=(132.249,-237.479,0) rot=(0,0,1;5.23599rad)
  Rows = 1
FEATURE [Part::Part2DObjectPython] Circle146  # Draft 2D object (typed FeaturePython)
  Area = 0
  FirstAngle = 0
  LastAngle = 0
  MakeFace = false
  Placement = pos=(135.895,-235.374,0) rot=(0,0,1;5.23599rad)
  Radius = 1
FEATURE [Part::Part2DObjectPython] Rectangle147  # Draft 2D object (typed FeaturePython)
  Area = 0
  ChamferSize = 0
  Columns = 1
  FilletRadius = 0
  Height = 6
  Length = 6
  MakeFace = false
  Placement = pos=(141.016,-236.036,0) rot=(0,0,1;3.13636rad)
  Rows = 1
FEATURE [Part::Part2DObjectPython] Circle147  # Draft 2D object (typed FeaturePython)
  Area = 3.14159
  FirstAngle = 0
  LastAngle = 0
  MakeFace = true
  Placement = pos=(134,-238.999,0) rot=(0,0,1;3.13636rad)
  Radius = 1
FEATURE [Part::Part2DObjectPython] Rectangle148  # Draft 2D object (typed FeaturePython)
  Area = 0
  ChamferSize = 0
  Columns = 1
  FilletRadius = 0
  Height = 8.42
  Length = 8.42
  MakeFace = false
  Placement = pos=(145.332,-229.703,0) rot=(0,0,1;5.29199rad)
  Rows = 1
FEATURE [Part::Part2DObjectPython] Circle148  # Draft 2D object (typed FeaturePython)
  Area = 0
  FirstAngle = 0
  LastAngle = 0
  MakeFace = false
  Placement = pos=(148.854,-227.398,0) rot=(0,0,1;5.29199rad)
  Radius = 1
FEATURE [Part::Part2DObjectPython] Rectangle149  # Draft 2D object (typed FeaturePython)
  Area = 0
  ChamferSize = 0
  Columns = 1
  FilletRadius = 0
  Height = 6
  Length = 6
  MakeFace = false
  Placement = pos=(153.592,-227.443,0) rot=(0,0,1;3.31665rad)
  Rows = 1
FEATURE [Part::Part2DObjectPython] Circle149  # Draft 2D object (typed FeaturePython)
  Area = 3.14159
  FirstAngle = 0
  LastAngle = 0
  MakeFace = true
  Placement = pos=(147.221,-231.617,0) rot=(0,0,1;3.31665rad)
  Radius = 1
FEATURE [Part::Part2DObjectPython] Rectangle150  # Draft 2D object (typed FeaturePython)
  Area = 0
  ChamferSize = 0
  Columns = 1
  FilletRadius = 0
  Height = 8.42
  Length = 8.42
  MakeFace = false
  Placement = pos=(157.963,-221.211,0) rot=(0,0,1;5.34799rad)
  Rows = 1
FEATURE [Part::Part2DObjectPython] Circle150  # Draft 2D object (typed FeaturePython)
  Area = 0
  FirstAngle = 0
  LastAngle = 0
  MakeFace = false
  Placement = pos=(161.351,-218.712,0) rot=(0,0,1;5.34799rad)
  Radius = 1
FEATURE [Part::Part2DObjectPython] Rectangle151  # Draft 2D object (typed FeaturePython)
  Area = 0
  ChamferSize = 0
  Columns = 1
  FilletRadius = 0
  Height = 6
  Length = 6
  MakeFace = false
  Placement = pos=(165.62,-218.244,0) rot=(0,0,1;3.49659rad)
  Rows = 1
FEATURE [Part::Part2DObjectPython] Circle151  # Draft 2D object (typed FeaturePython)
  Area = 3.14159
  FirstAngle = 0
  LastAngle = 0
  MakeFace = true
  Placement = pos=(160.099,-223.49,0) rot=(0,0,1;3.49659rad)
  Radius = 1
FEATURE [Part::Part2DObjectPython] Rectangle152  # Draft 2D object (typed FeaturePython)
  Area = 0
  ChamferSize = 0
  Columns = 1
  FilletRadius = 0
  Height = 8.42
  Length = 8.42
  MakeFace = false
  Placement = pos=(170.092,-212.022,0) rot=(0,0,1;5.40398rad)
  Rows = 1
FEATURE [Part::Part2DObjectPython] Circle152  # Draft 2D object (typed FeaturePython)
  Area = 0
  FirstAngle = 0
  LastAngle = 0
  MakeFace = false
  Placement = pos=(173.335,-209.337,0) rot=(0,0,1;5.40398rad)
  Radius = 1
FEATURE [Part::Part2DObjectPython] Rectangle153  # Draft 2D object (typed FeaturePython)
  Area = 0
  ChamferSize = 0
  Columns = 1
  FilletRadius = 0
  Height = 6
  Length = 6
  MakeFace = false
  Placement = pos=(177.079,-208.472,0) rot=(0,0,1;3.67479rad)
  Rows = 1
FEATURE [Part::Part2DObjectPython] Circle153  # Draft 2D object (typed FeaturePython)
  Area = 3.14159
  FirstAngle = 0
  LastAngle = 0
  MakeFace = true
  Placement = pos=(172.575,-214.613,0) rot=(0,0,1;3.67479rad)
  Radius = 1
FEATURE [Part::Part2DObjectPython] Rectangle154  # Draft 2D object (typed FeaturePython)
  Area = 0
  ChamferSize = 0
  Columns = 1
  FilletRadius = 0
  Height = 8.42
  Length = 8.42
  MakeFace = false
  Placement = pos=(206.652,-176.578,0) rot=(0,0,1;5.59159rad)
  Rows = 1
FEATURE [Part::Part2DObjectPython] Circle154  # Draft 2D object (typed FeaturePython)
  Area = 0
  FirstAngle = 0
  LastAngle = 0
  MakeFace = false
  Placement = pos=(209.337,-173.335,0) rot=(0,0,1;5.59159rad)
  Radius = 1
FEATURE [Part::Part2DObjectPython] Rectangle155  # Draft 2D object (typed FeaturePython)
  Area = 0
  ChamferSize = 0
  Columns = 1
  FilletRadius = 0
  Height = 6
  Length = 6
  MakeFace = false
  Placement = pos=(211.679,-171.874,0) rot=(0,0,1;4.14097rad)
  Rows = 1
FEATURE [App::FeaturePython] Text022  # WARN: FeaturePython — macro-defined, semantics opaque (R4)
  Placement = pos=(207.836,-181.597,0) rot=(0,0,-1;5.26252rad)
  Text = 0
FEATURE [App::FeaturePython] Text023  # WARN: FeaturePython — macro-defined, semantics opaque (R4)
  Placement = pos=(256.902,-91.1209,0) rot=(0,0,1;2.1005rad)
  Text = 5
FEATURE [Part::Part2DObjectPython] Circle155  # Draft 2D object (typed FeaturePython)
  Area = 3.14159
  FirstAngle = 0
  LastAngle = 0
  MakeFace = true
  Placement = pos=(210.417,-179.385,0) rot=(0,0,1;4.14097rad)
  Radius = 1
FEATURE [Part::Part2DObjectPython] Rectangle156  # Draft 2D object (typed FeaturePython)
  Area = 0
  ChamferSize = 0
  Columns = 1
  FilletRadius = 0
  Height = 8.42
  Length = 8.42
  MakeFace = false
  Placement = pos=(216.213,-164.739,0) rot=(0,0,1;5.64758rad)
  Rows = 1
FEATURE [Part::Part2DObjectPython] Circle156  # Draft 2D object (typed FeaturePython)
  Area = 0
  FirstAngle = 0
  LastAngle = 0
  MakeFace = false
  Placement = pos=(218.712,-161.351,0) rot=(0,0,1;5.64758rad)
  Radius = 1
FEATURE [Part::Part2DObjectPython] Rectangle157  # Draft 2D object (typed FeaturePython)
  Area = 0
  ChamferSize = 0
  Columns = 1
  FilletRadius = 0
  Height = 6
  Length = 6
  MakeFace = false
  Placement = pos=(224.524,-160.368,0) rot=(0,0,1;3.31874rad)
  Rows = 1
FEATURE [Part::Part2DObjectPython] Circle157  # Draft 2D object (typed FeaturePython)
  Area = 3.14159
  FirstAngle = 0
  LastAngle = 0
  MakeFace = true
  Placement = pos=(218.163,-164.555,0) rot=(0,0,1;3.31874rad)
  Radius = 1
FEATURE [Part::Part2DObjectPython] Rectangle158  # Draft 2D object (typed FeaturePython)
  Area = 0
  ChamferSize = 0
  Columns = 1
  FilletRadius = 0
  Height = 8.42
  Length = 8.42
  MakeFace = false
  Placement = pos=(225.092,-152.377,0) rot=(0,0,1;5.70358rad)
  Rows = 1
FEATURE [Part::Part2DObjectPython] Circle158  # Draft 2D object (typed FeaturePython)
  Area = 0
  FirstAngle = 0
  LastAngle = 0
  MakeFace = false
  Placement = pos=(227.398,-148.854,0) rot=(0,0,1;5.70358rad)
  Radius = 1
FEATURE [Part::Part2DObjectPython] Rectangle159  # Draft 2D object (typed FeaturePython)
  Area = 0
  ChamferSize = 0
  Columns = 1
  FilletRadius = 0
  Height = 6
  Length = 6
  MakeFace = false
  Placement = pos=(233.417,-154.59,0) rot=(0,0,1;1.41476rad)
  Rows = 1
FEATURE [Part::Part2DObjectPython] Circle159  # Draft 2D object (typed FeaturePython)
  Area = 3.14159
  FirstAngle = 0
  LastAngle = 0
  MakeFace = true
  Placement = pos=(231.542,-147.209,0) rot=(0,0,1;1.41476rad)
  Radius = 1
FEATURE [Part::Part2DObjectPython] Rectangle160  # Draft 2D object (typed FeaturePython)
  Area = 0
  ChamferSize = 0
  Columns = 1
  FilletRadius = 0
  Height = 8.42
  Length = 8.42
  MakeFace = false
  Placement = pos=(233.269,-139.541,0) rot=(0,0,1;5.75958rad)
  Rows = 1
FEATURE [Part::Part2DObjectPython] Circle160  # Draft 2D object (typed FeaturePython)
  Area = 0
  FirstAngle = 0
  LastAngle = 0
  MakeFace = false
  Placement = pos=(235.374,-135.895,0) rot=(0,0,1;5.75958rad)
  Radius = 1
FEATURE [Part::Part2DObjectPython] Rectangle161  # Draft 2D object (typed FeaturePython)
  Area = 0
  ChamferSize = 0
  Columns = 1
  FilletRadius = 0
  Height = 6
  Length = 6
  MakeFace = false
  Placement = pos=(241.673,-141.311,0) rot=(0,0,1;1.46084rad)
  Rows = 1
FEATURE [Part::Part2DObjectPython] Circle161  # Draft 2D object (typed FeaturePython)
  Area = 3.14159
  FirstAngle = 0
  LastAngle = 0
  MakeFace = true
  Placement = pos=(239.459,-134.024,0) rot=(0,0,1;1.46084rad)
  Radius = 1
FEATURE [Part::Part2DObjectPython] Rectangle162  # Draft 2D object (typed FeaturePython)
  Area = 0
  ChamferSize = 0
  Columns = 1
  FilletRadius = 0
  Height = 8.42
  Length = 8.42
  MakeFace = false
  Placement = pos=(240.714,-126.27,0) rot=(0,0,1;5.81557rad)
  Rows = 1
FEATURE [Part::Part2DObjectPython] Circle162  # Draft 2D object (typed FeaturePython)
  Area = 0
  FirstAngle = 0
  LastAngle = 0
  MakeFace = false
  Placement = pos=(242.612,-122.512,0) rot=(0,0,1;5.81557rad)
  Radius = 1
FEATURE [Part::Part2DObjectPython] Rectangle163  # Draft 2D object (typed FeaturePython)
  Area = 0
  ChamferSize = 0
  Columns = 1
  FilletRadius = 0
  Height = 6
  Length = 6
  MakeFace = false
  Placement = pos=(249.26,-127.516,0) rot=(0,0,1;1.53484rad)
  Rows = 1
FEATURE [Part::Part2DObjectPython] Circle163  # Draft 2D object (typed FeaturePython)
  Area = 3.14159
  FirstAngle = 0
  LastAngle = 0
  MakeFace = true
  Placement = pos=(246.514,-120.413,0) rot=(0,0,1;1.53484rad)
  Radius = 1
FEATURE [Part::Part2DObjectPython] Rectangle164  # Draft 2D object (typed FeaturePython)
  Area = 0
  ChamferSize = 0
  Columns = 1
  FilletRadius = 0
  Height = 8.42
  Length = 8.42
  MakeFace = false
  Placement = pos=(247.407,-112.594,0) rot=(0,0,1;5.87159rad)
  Rows = 1
FEATURE [Part::Part2DObjectPython] Circle164  # Draft 2D object (typed FeaturePython)
  Area = 0
  FirstAngle = 0
  LastAngle = 0
  MakeFace = false
  Placement = pos=(249.092,-108.736,0) rot=(0,0,1;5.87159rad)
  Radius = 1
FEATURE [Part::Part2DObjectPython] Rectangle165  # Draft 2D object (typed FeaturePython)
  Area = 0
  ChamferSize = 0
  Columns = 1
  FilletRadius = 0
  Height = 6
  Length = 6
  MakeFace = false
  Placement = pos=(256.074,-113.29,0) rot=(0,0,1;1.61321rad)
  Rows = 1
FEATURE [Part::Part2DObjectPython] Circle165  # Draft 2D object (typed FeaturePython)
  Area = 3.14159
  FirstAngle = 0
  LastAngle = 0
  MakeFace = true
  Placement = pos=(252.78,-106.424,0) rot=(0,0,1;1.61321rad)
  Radius = 1
FEATURE [Part::Part2DObjectPython] Rectangle166  # Draft 2D object (typed FeaturePython)
  Area = 0
  ChamferSize = 0
  Columns = 1
  FilletRadius = 0
  Height = 8.42
  Length = 8.42
  MakeFace = false
  Placement = pos=(253.318,-98.5709,0) rot=(0,0,1;5.92758rad)
  Rows = 1
FEATURE [Part::Part2DObjectPython] Circle166  # Draft 2D object (typed FeaturePython)
  Area = 0
  FirstAngle = 0
  LastAngle = 0
  MakeFace = false
  Placement = pos=(254.783,-94.6243,0) rot=(0,0,1;5.92758rad)
  Radius = 1
FEATURE [Part::Part2DObjectPython] Rectangle167  # Draft 2D object (typed FeaturePython)
  Area = 0
  ChamferSize = 0
  Columns = 1
  FilletRadius = 0
  Height = 6
  Length = 6
  MakeFace = false
  Placement = pos=(262.079,-98.695,0) rot=(0,0,1;1.69506rad)
  Rows = 1
FEATURE [Part::Part2DObjectPython] Circle167  # Draft 2D object (typed FeaturePython)
  Area = 3.14159
  FirstAngle = 0
  LastAngle = 0
  MakeFace = true
  Placement = pos=(258.234,-92.1208,0) rot=(0,0,1;1.69506rad)
  Radius = 1
FEATURE [App::DocumentObjectGroup] Everything
  Group = -> [Rectangle,Circle,Rectangle001,Circle001,Rectangle002,Circle002,Rectangle003,Circle003,Rectangle004,Circle004,Rectangle005,Circle005,Rectangle006,Circle006,Rectangle007,Circle007,Rectangle008,Circle008,Rectangle009,Circle009,Rectangle010,Circle010,Rectangle011,Circle011,Rectangle012,Circle012,Rectangle013,Circle013,Rectangle014,Circle014,Rectangle015,Circle015,Rectangle016,Circle016,Rectangle017,+301 more]
